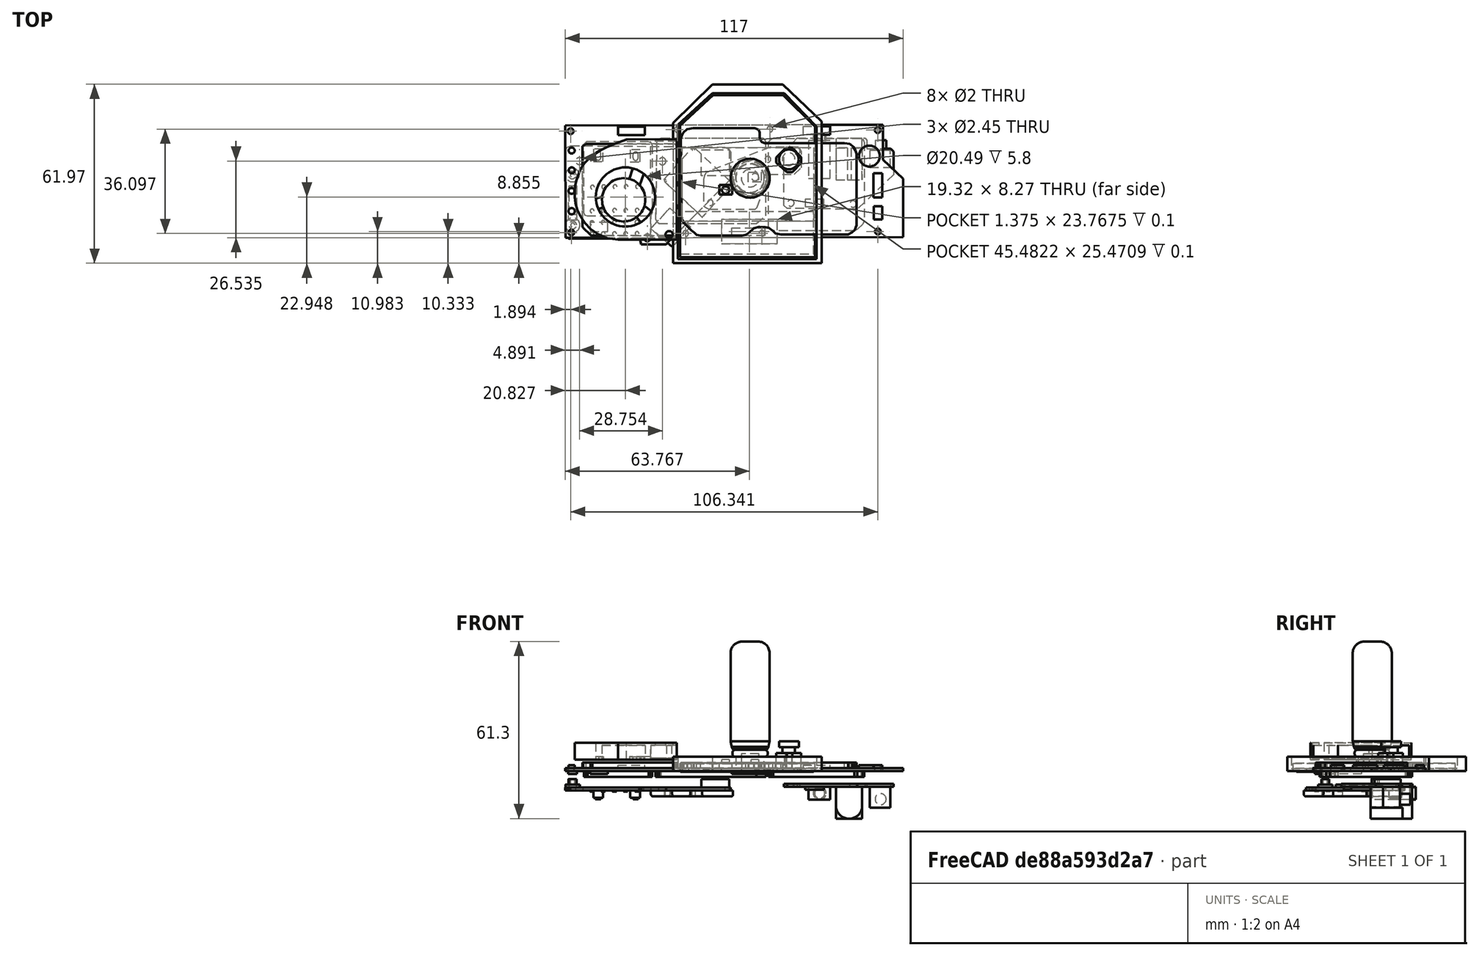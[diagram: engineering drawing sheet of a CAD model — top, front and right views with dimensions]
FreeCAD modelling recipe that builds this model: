
FCSTD DOCUMENT  (FreeCAD 0.19R24267 +99 (Git))
Label: v2PCB
License: All rights reserved
LicenseURL: http://en.wikipedia.org/wiki/All_rights_reserved
objects: Sketcher::SketchObject×41, PartDesign::Pad×35, Image::ImagePlane×9, PartDesign::Pocket×9, PartDesign::Body×8, PartDesign::Fillet×6, PartDesign::Chamfer×3, Mesh::Feature×1
note: 155 computed .brp shape members not serialized (recipe doc carries the construction recipe); baked Part::Feature solids carry a one-line shape summary decoded from their .brp

FEATURE [Image::ImagePlane] ImagePlane
  Placement = pos=(0,0,0) rot=(0,0,1;0.003491rad)
  XSize = 195.643
  YSize = 146.825
FEATURE [Sketcher::SketchObject] Sketch
  FullyConstrained = false
  MapMode = 5
  Support = -> [XY_Plane]
  sketch-geometry (14):
    g0: LineSegment StartX=-53.023 StartY=20.4074 StartZ=0 EndX=-52.9788 EndY=0.202758 EndZ=0
    g1: LineSegment StartX=-52.9788 StartY=0.202758 StartZ=0 EndX=-46.0602 EndY=-6.3752 EndZ=0
    g2: LineSegment StartX=-46.0602 StartY=-6.3752 StartZ=0 EndX=-46.0602 EndY=-18.4974 EndZ=0
    g3: LineSegment StartX=-46.0602 StartY=-18.4974 StartZ=0 EndX=63.9761 EndY=-18.2567 EndZ=0
    g4: LineSegment StartX=63.9761 StartY=-18.2567 StartZ=0 EndX=63.8909 EndY=20.6632 EndZ=0
    g5: LineSegment StartX=63.8909 StartY=20.6632 StartZ=0 EndX=-53.023 EndY=20.4074 EndZ=0
    g6: Circle CenterX=-44.2552 CenterY=18.4624 CenterZ=0 NormalX=0 NormalY=0 NormalZ=1 AngleXU=0 Radius=1
    g7: Circle CenterX=61.8709 CenterY=18.8233 CenterZ=0 NormalX=0 NormalY=0 NormalZ=1 AngleXU=0 Radius=1
    g8: Circle CenterX=62.0861 CenterY=-16.2831 CenterZ=0 NormalX=0 NormalY=0 NormalZ=1 AngleXU=0 Radius=1
    g9: Circle CenterX=25.1233 CenterY=-16.8581 CenterZ=0 NormalX=0 NormalY=0 NormalZ=1 AngleXU=0 Radius=1
    g10: Circle CenterX=-6.87654 CenterY=-16.9797 CenterZ=0 NormalX=0 NormalY=0 NormalZ=1 AngleXU=0 Radius=1
    g11: Circle CenterX=-44.1832 CenterY=-16.667 CenterZ=0 NormalX=0 NormalY=0 NormalZ=1 AngleXU=0 Radius=1
    g12: Circle CenterX=-4.12317 CenterY=19.0574 CenterZ=0 NormalX=0 NormalY=0 NormalZ=1 AngleXU=0 Radius=1
    g13: Circle CenterX=22.3007 CenterY=19.1172 CenterZ=0 NormalX=0 NormalY=0 NormalZ=1 AngleXU=0 Radius=1
  constraints (12):
    c: Coincident(g0,g1)
    c: Coincident(g1,g2)
    c: Vertical(g2)
    c: Coincident(g2,g3)
    c: Coincident(g3,g4)
    c: Coincident(g4,g5)
    c: Coincident(g5,g0)
    c: Parallel(g5,g3)
    c: DistanceX(g0) = -53.023
    c: DistanceY(g0) = 20.4074
    c: Perpendicular(g5,g0)
    c: Parallel(g4,g0)
FEATURE [PartDesign::Pad] Pad
  Direction = (1,1,1)
  Length = 1.1
  Length2 = 100
  Profile = -> Sketch
  Type = 0
FEATURE [Sketcher::SketchObject] Sketch001
  FullyConstrained = false
  MapMode = 5
  Support = -> [XY_Plane]
  sketch-geometry (61):
    g0: LineSegment StartX=-36.8446 StartY=16.2765 StartZ=0 EndX=-36.1772 EndY=17.9834 EndZ=0
    g1: LineSegment StartX=-36.1772 StartY=17.9834 StartZ=0 EndX=-35.306 EndY=18.7577 EndZ=0
    g2: LineSegment StartX=-35.306 StartY=18.7577 StartZ=0 EndX=-33.9509 EndY=19.5321 EndZ=0
    g3: LineSegment StartX=-33.9509 StartY=19.5321 StartZ=0 EndX=-10.7286 EndY=19.5321 EndZ=0
    g4: LineSegment StartX=-10.7286 StartY=19.5321 StartZ=0 EndX=-8.78697 EndY=19.1207 EndZ=0
    g5: LineSegment StartX=-8.78697 StartY=19.1207 StartZ=0 EndX=-7.91522 EndY=18.249 EndZ=0
    g6: LineSegment StartX=-7.91522 StartY=18.249 StartZ=0 EndX=-6.44909 EndY=17.1791 EndZ=0
    g7: LineSegment StartX=-6.44909 StartY=17.1791 StartZ=0 EndX=-5.18108 EndY=16.9413 EndZ=0
    g8: LineSegment StartX=-5.18108 StartY=16.9413 StartZ=0 EndX=-3.1602 EndY=16.8225 EndZ=0
    g9: LineSegment StartX=-3.1602 StartY=16.8225 StartZ=0 EndX=-1.29782 EndY=17.3772 EndZ=0
    g10: LineSegment StartX=-1.29782 StartY=17.3772 StartZ=0 EndX=0.401002 EndY=18.8142 EndZ=0
    g11: LineSegment StartX=0.401002 StartY=18.8142 StartZ=0 EndX=1.4716 EndY=19.5604 EndZ=0
    g12: LineSegment StartX=1.4716 StartY=19.5604 StartZ=0 EndX=2.70441 EndY=19.8848 EndZ=0
    g13: LineSegment StartX=2.70441 StartY=19.8848 StartZ=0 EndX=17.0749 EndY=19.8848 EndZ=0
    g14: LineSegment StartX=17.0749 StartY=19.8848 StartZ=0 EndX=18.5348 EndY=19.5644 EndZ=0
    g15: LineSegment StartX=18.5348 StartY=19.5644 StartZ=0 EndX=19.3134 EndY=18.9155 EndZ=0
    g16: LineSegment StartX=19.3134 StartY=18.9155 StartZ=0 EndX=20.3191 EndY=18.1044 EndZ=0
    g17: LineSegment StartX=20.3191 StartY=18.1044 StartZ=0 EndX=21.5195 EndY=16.8716 EndZ=0
    g18: LineSegment StartX=21.5195 StartY=16.8716 StartZ=0 EndX=22.8498 EndY=15.569 EndZ=0
    g19: LineSegment StartX=22.8498 StartY=15.569 StartZ=0 EndX=23.4607 EndY=14.5331 EndZ=0
    g20: LineSegment StartX=23.4607 StartY=14.5331 StartZ=0 EndX=23.7263 EndY=13.0722 EndZ=0
    g21: LineSegment StartX=23.7263 StartY=13.0722 StartZ=0 EndX=25.0278 EndY=13.0722 EndZ=0
    g22: LineSegment StartX=25.0278 StartY=13.0722 StartZ=0 EndX=25.0278 EndY=18.1699 EndZ=0
    g23: LineSegment StartX=25.0278 StartY=18.1699 StartZ=0 EndX=25.2082 EndY=19.0134 EndZ=0
    g24: LineSegment StartX=25.2082 StartY=19.0134 StartZ=0 EndX=25.6624 EndY=19.565 EndZ=0
    g25: LineSegment StartX=25.6624 StartY=19.565 StartZ=0 EndX=26.2464 EndY=19.8894 EndZ=0
    g26: LineSegment StartX=26.2464 StartY=19.8894 StartZ=0 EndX=54.5296 EndY=19.8894 EndZ=0
    g27: LineSegment StartX=54.5296 StartY=19.8894 StartZ=0 EndX=54.9473 EndY=19.84 EndZ=0
    g28: LineSegment StartX=54.9473 StartY=19.84 StartZ=0 EndX=55.2696 EndY=19.6371 EndZ=0
    g29: LineSegment StartX=55.2696 StartY=19.6371 StartZ=0 EndX=57.764 EndY=17.2382 EndZ=0
    g30: LineSegment StartX=57.764 StartY=17.2382 StartZ=0 EndX=58.0385 EndY=16.6415 EndZ=0
    g31: LineSegment StartX=58.0385 StartY=16.6415 StartZ=0 EndX=58.0623 EndY=16.2476 EndZ=0
    g32: LineSegment StartX=58.0623 StartY=16.2476 StartZ=0 EndX=58.0623 EndY=-10.4127 EndZ=0
    g33: LineSegment StartX=58.0623 StartY=-10.4127 StartZ=0 EndX=57.9614 EndY=-11.0869 EndZ=0
    g34: LineSegment StartX=57.9614 StartY=-11.0869 StartZ=0 EndX=57.5315 EndY=-11.4289 EndZ=0
    g35: LineSegment StartX=57.5315 StartY=-11.4289 StartZ=0 EndX=56.7107 EndY=-11.8882 EndZ=0
    g36: LineSegment StartX=56.7107 StartY=-11.8882 StartZ=0 EndX=26.8243 EndY=-11.8882 EndZ=0
    g37: LineSegment StartX=26.8243 StartY=-11.8882 StartZ=0 EndX=25.8681 EndY=-11.7722 EndZ=0
    g38: LineSegment StartX=25.8681 StartY=-11.7722 StartZ=0 EndX=25.3103 EndY=-11.0816 EndZ=0
    g39: LineSegment StartX=25.3103 StartY=-11.0816 StartZ=0 EndX=25.0978 EndY=-10.3645 EndZ=0
    g40: LineSegment StartX=25.0978 StartY=-10.3645 StartZ=0 EndX=23.9557 EndY=-10.4441 EndZ=0
    g41: LineSegment StartX=23.9557 StartY=-10.4441 StartZ=0 EndX=23.9557 EndY=-13.8325 EndZ=0
    g42: LineSegment StartX=23.9557 StartY=-13.8325 StartZ=0 EndX=23.6148 EndY=-14.7887 EndZ=0
    g43: LineSegment StartX=23.6148 StartY=-14.7887 StartZ=0 EndX=23.057 EndY=-15.8512 EndZ=0
    g44: LineSegment StartX=23.057 StartY=-15.8512 StartZ=0 EndX=21.8351 EndY=-16.9136 EndZ=0
    g45: LineSegment StartX=21.8351 StartY=-16.9136 StartZ=0 EndX=19.6168 EndY=-17.3676 EndZ=0
    g46: LineSegment StartX=19.6168 StartY=-17.3676 StartZ=0 EndX=16.8333 EndY=-17.3676 EndZ=0
    g47: LineSegment StartX=16.8333 StartY=-17.3676 StartZ=0 EndX=4.71408 EndY=-17.3676 EndZ=0
    g48: LineSegment StartX=4.71408 StartY=-17.3676 StartZ=0 EndX=-1.58584 EndY=-17.3676 EndZ=0
    g49: LineSegment StartX=-1.58584 StartY=-17.3676 StartZ=0 EndX=-2.89259 EndY=-16.8664 EndZ=0
    g50: LineSegment StartX=-2.89259 StartY=-16.8664 StartZ=0 EndX=-3.37658 EndY=-15.8501 EndZ=0
    g51: LineSegment StartX=-3.37658 StartY=-15.8501 StartZ=0 EndX=-3.37658 EndY=-14.1227 EndZ=0
    g52: LineSegment StartX=-3.37658 StartY=-14.1227 StartZ=0 EndX=-3.59208 EndY=-13.1169 EndZ=0
    g53: LineSegment StartX=-3.59208 StartY=-13.1169 StartZ=0 EndX=-4.1436 EndY=-12.533 EndZ=0
    g54: LineSegment StartX=-4.1436 StartY=-12.533 StartZ=0 EndX=-5.14931 EndY=-12.1437 EndZ=0
    g55: LineSegment StartX=-5.14931 StartY=-12.1437 StartZ=0 EndX=-32.6772 EndY=-12.1437 EndZ=0
    g56: LineSegment StartX=-32.6772 StartY=-12.1437 StartZ=0 EndX=-34.5589 EndY=-11.868 EndZ=0
    g57: LineSegment StartX=-34.5589 StartY=-11.868 StartZ=0 EndX=-35.6619 EndY=-10.8947 EndZ=0
    g58: LineSegment StartX=-35.6619 StartY=-10.8947 StartZ=0 EndX=-36.5054 EndY=-9.5646 EndZ=0
    g59: LineSegment StartX=-36.5054 StartY=-9.5646 StartZ=0 EndX=-36.8446 EndY=-8.44037 EndZ=0
    g60: LineSegment StartX=-36.8446 StartY=-8.44037 StartZ=0 EndX=-36.8446 EndY=16.2765 EndZ=0
  constraints (75):
    c: Coincident(g0,g1)
    c: Coincident(g1,g2)
    c: Coincident(g2,g3)
    c: Horizontal(g3)
    c: Coincident(g3,g4)
    c: Coincident(g4,g5)
    c: Coincident(g5,g6)
    c: Coincident(g6,g7)
    c: Coincident(g7,g8)
    c: Coincident(g8,g9)
    c: Coincident(g9,g10)
    c: Coincident(g10,g11)
    c: Coincident(g11,g12)
    c: Coincident(g12,g13)
    c: Horizontal(g13)
    c: Coincident(g13,g14)
    c: Coincident(g14,g15)
    c: Coincident(g15,g16)
    c: Coincident(g16,g17)
    c: Coincident(g17,g18)
    c: Coincident(g18,g19)
    c: Coincident(g19,g20)
    c: Coincident(g20,g21)
    c: Horizontal(g21)
    c: Coincident(g21,g22)
    c: Vertical(g22)
    c: Coincident(g22,g23)
    c: Coincident(g23,g24)
    c: Coincident(g24,g25)
    c: Coincident(g25,g26)
    c: Horizontal(g26)
    c: Coincident(g26,g27)
    c: Coincident(g27,g28)
    c: Coincident(g28,g29)
    c: Coincident(g29,g30)
    c: Coincident(g30,g31)
    c: Coincident(g31,g32)
    c: Vertical(g32)
    c: Coincident(g32,g33)
    c: Coincident(g33,g34)
    c: Coincident(g34,g35)
    c: Coincident(g35,g36)
    c: Horizontal(g36)
    c: Coincident(g36,g37)
    c: Coincident(g37,g38)
    c: Coincident(g38,g39)
    c: Coincident(g39,g40)
    c: Coincident(g40,g41)
    c: Vertical(g41)
    c: Coincident(g41,g42)
    c: Coincident(g42,g43)
    c: Coincident(g43,g44)
    c: Coincident(g44,g45)
    c: Coincident(g45,g46)
    c: Horizontal(g46)
    c: Coincident(g46,g47)
    c: Horizontal(g47)
    c: Coincident(g47,g48)
    c: Horizontal(g48)
    c: Coincident(g48,g49)
    c: Coincident(g49,g50)
    c: Coincident(g50,g51)
    c: Vertical(g51)
    c: Coincident(g51,g52)
    c: Coincident(g52,g53)
    c: Coincident(g53,g54)
    c: Coincident(g54,g55)
    c: Horizontal(g55)
    c: Coincident(g55,g56)
    c: Coincident(g56,g57)
    c: Coincident(g57,g58)
    c: Coincident(g58,g59)
    c: Coincident(g59,g60)
    c: Coincident(g60,g0)
    c: Vertical(g60)
FEATURE [PartDesign::Pad] Pad001
  BaseFeature = -> Pad
  Direction = (1,1,1)
  Length = 3
  Length2 = 100
  Profile = -> Sketch001
  Type = 0
FEATURE [Sketcher::SketchObject] Sketch002
  FullyConstrained = false
  MapMode = 5
  Placement = pos=(0,0,1.1) rot=(0,0,1;0rad)
  Support = -> [Pad001]
  sketch-geometry (21):
    g0: LineSegment StartX=-45.7157 StartY=14.2806 StartZ=0 EndX=-42.7834 EndY=14.2806 EndZ=0
    g1: LineSegment StartX=-42.7834 StartY=14.2806 StartZ=0 EndX=-42.7834 EndY=9.68408 EndZ=0
    g2: LineSegment StartX=-42.7834 StartY=9.68408 StartZ=0 EndX=-45.7157 EndY=9.68408 EndZ=0
    g3: LineSegment StartX=-45.7157 StartY=9.68408 StartZ=0 EndX=-45.7157 EndY=14.2806 EndZ=0
    g4: LineSegment StartX=-45.7553 StartY=6.63294 StartZ=0 EndX=-42.7042 EndY=6.63294 EndZ=0
    g5: LineSegment StartX=-42.7042 StartY=6.63294 StartZ=0 EndX=-42.7042 EndY=-1.68834 EndZ=0
    g6: LineSegment StartX=-42.7042 StartY=-1.68834 StartZ=0 EndX=-45.7553 EndY=-1.68834 EndZ=0
    g7: LineSegment StartX=-45.7553 StartY=-1.68834 StartZ=0 EndX=-45.7553 EndY=6.63294 EndZ=0
    g8: Circle CenterX=-41.3019 CenterY=-7.65171 CenterZ=0 NormalX=0 NormalY=0 NormalZ=1 AngleXU=0 Radius=3.62162
    g9: Circle CenterX=61.7609 CenterY=11.4352 CenterZ=0 NormalX=0 NormalY=0 NormalZ=1 AngleXU=0 Radius=1.0872
    g10: Circle CenterX=61.7934 CenterY=4.39516 CenterZ=0 NormalX=0 NormalY=0 NormalZ=1 AngleXU=0 Radius=1.03866
    g11: Circle CenterX=61.7273 CenterY=-2.72566 CenterZ=0 NormalX=0 NormalY=0 NormalZ=1 AngleXU=0 Radius=1.03866
    g12: Circle CenterX=61.7408 CenterY=-9.57455 CenterZ=0 NormalX=0 NormalY=0 NormalZ=1 AngleXU=0 Radius=1.03866
    g13: LineSegment StartX=-27.7059 StartY=-15.0443 StartZ=0 EndX=-18.4201 EndY=-15.0443 EndZ=0
    g14: LineSegment StartX=-18.4201 StartY=-15.0443 StartZ=0 EndX=-18.4201 EndY=-17.9821 EndZ=0
    g15: LineSegment StartX=-18.4201 StartY=-17.9821 StartZ=0 EndX=-27.7059 EndY=-17.9821 EndZ=0
    g16: LineSegment StartX=-27.7059 StartY=-17.9821 StartZ=0 EndX=-27.7059 EndY=-15.0443 EndZ=0
    g17: LineSegment StartX=36.3929 StartY=-14.8666 StartZ=0 EndX=45.7202 EndY=-14.8666 EndZ=0
    g18: LineSegment StartX=45.7202 StartY=-14.8666 StartZ=0 EndX=45.7202 EndY=-17.8222 EndZ=0
    g19: LineSegment StartX=45.7202 StartY=-17.8222 StartZ=0 EndX=36.3929 EndY=-17.8222 EndZ=0
    g20: LineSegment StartX=36.3929 StartY=-17.8222 StartZ=0 EndX=36.3929 EndY=-14.8666 EndZ=0
  constraints (32):
    c: Coincident(g0,g1)
    c: Coincident(g1,g2)
    c: Coincident(g2,g3)
    c: Coincident(g3,g0)
    c: Horizontal(g0)
    c: Horizontal(g2)
    c: Vertical(g1)
    c: Vertical(g3)
    c: Coincident(g4,g5)
    c: Coincident(g5,g6)
    c: Coincident(g6,g7)
    c: Coincident(g7,g4)
    c: Horizontal(g4)
    c: Horizontal(g6)
    c: Vertical(g5)
    c: Vertical(g7)
    c: Coincident(g13,g14)
    c: Coincident(g14,g15)
    c: Coincident(g15,g16)
    c: Coincident(g16,g13)
    c: Horizontal(g13)
    c: Horizontal(g15)
    c: Vertical(g14)
    c: Vertical(g16)
    c: Coincident(g17,g18)
    c: Coincident(g18,g19)
    c: Coincident(g19,g20)
    c: Coincident(g20,g17)
    c: Horizontal(g17)
    c: Horizontal(g19)
    c: Vertical(g18)
    c: Vertical(g20)
FEATURE [PartDesign::Pad] Pad002
  BaseFeature = -> Pad001
  Direction = (1,1,1)
  Length = 1
  Length2 = 100
  Profile = -> Sketch002
  Type = 0
FEATURE [Sketcher::SketchObject] Sketch003
  FullyConstrained = false
  MapMode = 5
  Placement = pos=(0,0,3) rot=(0,0,1;0rad)
  Support = -> [Pad002]
  sketch-geometry (4):
    g0: LineSegment StartX=23.7352 StartY=13.1919 StartZ=0 EndX=23.9822 EndY=-10.5289 EndZ=0
    g1: LineSegment StartX=23.9822 StartY=-10.5289 StartZ=0 EndX=25.1102 EndY=-10.5289 EndZ=0
    g2: LineSegment StartX=25.1102 StartY=-10.5289 StartZ=0 EndX=25.0187 EndY=13.2386 EndZ=0
    g3: LineSegment StartX=25.0187 StartY=13.2386 StartZ=0 EndX=23.7352 EndY=13.1919 EndZ=0
  constraints (5):
    c: Coincident(g0,g1)
    c: Horizontal(g1)
    c: Coincident(g1,g2)
    c: Coincident(g2,g3)
    c: Coincident(g3,g0)
FEATURE [PartDesign::Pocket] Pocket
  BaseFeature = -> Pad002
  Length = 2
  Length2 = 100
  Profile = -> Sketch003
  Type = 0
FEATURE [Image::ImagePlane] ImagePlane001
  Placement = pos=(6.7,2,0) rot=(-1,0,0;3.14159rad)
  XSize = 196.671
  YSize = 147.597
FEATURE [Sketcher::SketchObject] Sketch004
  FullyConstrained = false
  MapMode = 5
  Placement = pos=(0,0,0) rot=(1,0,0;3.14159rad)
  Support = -> [Pocket]
  sketch-geometry (37):
    g0: LineSegment StartX=-38.3718 StartY=13.8148 StartZ=0 EndX=-39.0172 EndY=13.3602 EndZ=0
    g1: LineSegment StartX=-39.0172 StartY=13.3602 StartZ=0 EndX=-39.4107 EndY=12.8136 EndZ=0
    g2: LineSegment StartX=-39.4107 StartY=12.8136 StartZ=0 EndX=-39.52 EndY=12.4201 EndZ=0
    g3: LineSegment StartX=-39.52 StartY=12.4201 StartZ=0 EndX=-39.52 EndY=-14.6845 EndZ=0
    g4: LineSegment StartX=-39.52 StartY=-14.6845 StartZ=0 EndX=-38.9803 EndY=-15.9239 EndZ=0
    g5: LineSegment StartX=-38.9803 StartY=-15.9239 StartZ=0 EndX=-37.056 EndY=-17.6525 EndZ=0
    g6: LineSegment StartX=-37.056 StartY=-17.6525 StartZ=0 EndX=-36.1428 EndY=-18.1744 EndZ=0
    g7: LineSegment StartX=-36.1428 StartY=-18.1744 StartZ=0 EndX=-8.00073 EndY=-18.1744 EndZ=0
    g8: LineSegment StartX=-8.00073 StartY=-18.1744 StartZ=0 EndX=-7.08768 EndY=-17.713 EndZ=0
    g9: LineSegment StartX=-7.08768 StartY=-17.713 StartZ=0 EndX=-6.31843 EndY=-17.0145 EndZ=0
    g10: LineSegment StartX=-6.31843 StartY=-17.0145 StartZ=0 EndX=-6.31843 EndY=12.3493 EndZ=0
    g11: LineSegment StartX=-6.31843 StartY=12.3493 StartZ=0 EndX=-6.70782 EndY=12.9208 EndZ=0
    g12: LineSegment StartX=-6.70782 StartY=12.9208 StartZ=0 EndX=-7.17678 EndY=13.4337 EndZ=0
    g13: LineSegment StartX=-7.17678 StartY=13.4337 StartZ=0 EndX=-7.73367 EndY=13.8148 EndZ=0
    g14: LineSegment StartX=-7.73367 StartY=13.8148 StartZ=0 EndX=-38.3718 EndY=13.8148 EndZ=0
    g15: LineSegment StartX=-5.50407 StartY=12.5862 StartZ=0 EndX=-5.05245 EndY=13.2897 EndZ=0
    g16: LineSegment StartX=-5.05245 StartY=13.2897 StartZ=0 EndX=-4.55126 EndY=13.7372 EndZ=0
    g17: LineSegment StartX=-4.55126 StartY=13.7372 StartZ=0 EndX=30.8305 EndY=13.7372 EndZ=0
    g18: LineSegment StartX=30.8305 StartY=13.7372 StartZ=0 EndX=31.5738 EndY=13.5845 EndZ=0
    g19: LineSegment StartX=31.5738 StartY=13.5845 StartZ=0 EndX=32.339 EndY=12.6663 EndZ=0
    g20: LineSegment StartX=32.339 StartY=12.6663 StartZ=0 EndX=32.7019 EndY=-14.1785 EndZ=0
    g21: LineSegment StartX=32.7019 StartY=-14.1785 StartZ=0 EndX=32.2884 EndY=-15.0677 EndZ=0
    g22: LineSegment StartX=32.2884 StartY=-15.0677 StartZ=0 EndX=31.5123 EndY=-15.6473 EndZ=0
    g23: LineSegment StartX=31.5123 StartY=-15.6473 StartZ=0 EndX=-2.13722 EndY=-15.6473 EndZ=0
    g24: LineSegment StartX=-2.13722 StartY=-15.6473 StartZ=0 EndX=-5.50407 EndY=-13.009 EndZ=0
    g25: LineSegment StartX=-5.50407 StartY=-13.009 StartZ=0 EndX=-5.50407 EndY=12.5862 EndZ=0
    g26: LineSegment StartX=33.8245 StartY=-11.8303 StartZ=0 EndX=34.2779 EndY=-12.7966 EndZ=0
    g27: LineSegment StartX=34.2779 StartY=-12.7966 StartZ=0 EndX=35.0834 EndY=-13.1367 EndZ=0
    g28: LineSegment StartX=35.0834 StartY=-13.1367 StartZ=0 EndX=56.2902 EndY=-13.1367 EndZ=0
    g29: LineSegment StartX=56.2902 StartY=-13.1367 StartZ=0 EndX=57.1647 EndY=-12.835 EndZ=0
    g30: LineSegment StartX=57.1647 StartY=-12.835 StartZ=0 EndX=57.4926 EndY=-12.0261 EndZ=0
    g31: LineSegment StartX=57.4926 StartY=-12.0261 StartZ=0 EndX=57.4926 EndY=11.7012 EndZ=0
    g32: LineSegment StartX=57.4926 StartY=11.7012 StartZ=0 EndX=56.4474 EndY=12.796 EndZ=0
    g33: LineSegment StartX=56.4474 StartY=12.796 StartZ=0 EndX=35.3435 EndY=12.796 EndZ=0
    g34: LineSegment StartX=35.3435 StartY=12.796 StartZ=0 EndX=34.3766 EndY=12.3259 EndZ=0
    g35: LineSegment StartX=34.3766 StartY=12.3259 StartZ=0 EndX=33.8245 EndY=11.4115 EndZ=0
    g36: LineSegment StartX=33.8245 StartY=11.4115 StartZ=0 EndX=33.8245 EndY=-11.8303 EndZ=0
  constraints (48):
    c: Coincident(g0,g1)
    c: Coincident(g1,g2)
    c: Coincident(g2,g3)
    c: Vertical(g3)
    c: Coincident(g3,g4)
    c: Coincident(g4,g5)
    c: Coincident(g5,g6)
    c: Coincident(g6,g7)
    c: Horizontal(g7)
    c: Coincident(g7,g8)
    c: Coincident(g8,g9)
    c: Coincident(g9,g10)
    c: Vertical(g10)
    c: Coincident(g10,g11)
    c: Coincident(g11,g12)
    c: Coincident(g12,g13)
    c: Coincident(g13,g14)
    c: Coincident(g14,g0)
    c: Horizontal(g14)
    c: Coincident(g15,g16)
    c: Coincident(g16,g17)
    c: Horizontal(g17)
    c: Coincident(g17,g18)
    c: Coincident(g18,g19)
    c: Coincident(g19,g20)
    c: Coincident(g20,g21)
    c: Coincident(g21,g22)
    c: Coincident(g22,g23)
    c: Horizontal(g23)
    c: Coincident(g23,g24)
    c: Coincident(g24,g25)
    c: Coincident(g25,g15)
    c: Vertical(g25)
    c: Coincident(g26,g27)
    c: Coincident(g27,g28)
    c: Horizontal(g28)
    c: Coincident(g28,g29)
    c: Coincident(g29,g30)
    c: Coincident(g30,g31)
    c: Vertical(g31)
    c: Coincident(g31,g32)
    c: Coincident(g32,g33)
    c: Horizontal(g33)
    c: Coincident(g33,g34)
    c: Coincident(g34,g35)
    c: Coincident(g35,g36)
    c: Coincident(g36,g26)
    c: Vertical(g36)
FEATURE [PartDesign::Pad] Pad003
  BaseFeature = -> Pocket
  Direction = (1,1,1)
  Length = 2
  Length2 = 100
  Profile = -> Sketch004
  Type = 0
FEATURE [Sketcher::SketchObject] Sketch005
  FullyConstrained = false
  MapMode = 5
  Placement = pos=(0,0,0) rot=(1,0,0;3.14159rad)
  Support = -> [Pad003]
  sketch-geometry (8):
    g0: LineSegment StartX=59.9182 StartY=-3.71203 StartZ=0 EndX=62.984 EndY=-3.71203 EndZ=0
    g1: LineSegment StartX=62.984 StartY=-3.71203 StartZ=0 EndX=62.984 EndY=-14.3772 EndZ=0
    g2: LineSegment StartX=62.984 StartY=-14.3772 StartZ=0 EndX=59.9182 EndY=-14.3772 EndZ=0
    g3: LineSegment StartX=59.9182 StartY=-14.3772 StartZ=0 EndX=59.9182 EndY=-3.71203 EndZ=0
    g4: LineSegment StartX=49.2016 StartY=-15.2468 StartZ=0 EndX=55.3231 EndY=-15.2468 EndZ=0
    g5: LineSegment StartX=55.3231 StartY=-15.2468 StartZ=0 EndX=55.3231 EndY=-18.4388 EndZ=0
    g6: LineSegment StartX=55.3231 StartY=-18.4388 StartZ=0 EndX=49.2016 EndY=-18.4388 EndZ=0
    g7: LineSegment StartX=49.2016 StartY=-18.4388 StartZ=0 EndX=49.2016 EndY=-15.2468 EndZ=0
  constraints (16):
    c: Coincident(g0,g1)
    c: Coincident(g1,g2)
    c: Coincident(g2,g3)
    c: Coincident(g3,g0)
    c: Horizontal(g0)
    c: Horizontal(g2)
    c: Vertical(g1)
    c: Vertical(g3)
    c: Coincident(g4,g5)
    c: Coincident(g5,g6)
    c: Coincident(g6,g7)
    c: Coincident(g7,g4)
    c: Horizontal(g4)
    c: Horizontal(g6)
    c: Vertical(g5)
    c: Vertical(g7)
FEATURE [PartDesign::Pad] Pad004
  BaseFeature = -> Pad003
  Direction = (1,1,1)
  Length = 1
  Length2 = 100
  Profile = -> Sketch005
  Type = 0
FEATURE [PartDesign::Body] Body  label="主板"
  Group = -> [Sketch,Pad,Sketch001,Pad001,Sketch002,Pad002,Sketch003,Pocket,Sketch004,Pad003,Sketch005,Pad004]
  Origin = -> Origin
  Placement = pos=(0,0,0) rot=(0,0,1;3.14159rad)
  Tip = -> Pad004
FEATURE [Image::ImagePlane] ImagePlane002
  Placement = pos=(-0.07487,-3.89928,0) rot=(0,0,1;6.26399rad)
  XSize = 121.534
  YSize = 162.205
FEATURE [Sketcher::SketchObject] Sketch006
  FullyConstrained = false
  MapMode = 5
  Support = -> [XY_Plane001]
  sketch-geometry (18):
    g0: LineSegment StartX=-18.4256 StartY=-1.34093 StartZ=0 EndX=-18.4099 EndY=-21.5909 EndZ=0
    g1: LineSegment StartX=-18.4099 StartY=-21.5909 StartZ=0 EndX=16.4943 EndY=-21.5976 EndZ=0
    g2: LineSegment StartX=16.4943 StartY=-21.5976 StartZ=0 EndX=16.2785 EndY=-4.27596 EndZ=0
    g3-g9: Circle x7 (B-spline internal-alignment scaffolding for g10; pole/knot coordinates omitted)
    g10: BSplineCurve PolesCount=7 KnotsCount=5 Degree=3 IsPeriodic=0
    g11-g15: GeomPoint x5 (B-spline internal-alignment scaffolding for g10; pole/knot coordinates omitted)
    g16: Circle CenterX=-3.60227 CenterY=-3.84748 CenterZ=0 NormalX=0 NormalY=0 NormalZ=1 AngleXU=0 Radius=10.2437
    g17: Circle CenterX=-16.6253 CenterY=-18.983 CenterZ=0 NormalX=0 NormalY=0 NormalZ=1 AngleXU=0 Radius=1.2374
  constraints (8):
    c: Coincident(g0,g1)
    c: Coincident(g1,g2)
    c: Coincident(g10,g0)
    c: Weight(g3) = 1
    c: Equal(g3, g4-g9) x6
    c: Coincident(g10,g2)
    c: InternalAlignment(g3-g9 -> g10) x7
    c: InternalAlignment(g11-g15 -> g10) x5
FEATURE [PartDesign::Pad] Pad005
  Direction = (1,1,1)
  Length = 5.8
  Length2 = 100
  Profile = -> Sketch006
  Type = 0
FEATURE [Sketcher::SketchObject] Sketch007
  FullyConstrained = false
  MapMode = 5
  Support = -> [XY_Plane001]
  sketch-geometry (12):
    g0: LineSegment StartX=-8.07719 StartY=5.93515 StartZ=0 EndX=-7.1147 EndY=3.78717 EndZ=0
    g1: LineSegment StartX=-7.1147 StartY=3.78717 StartZ=0 EndX=-10.6829 EndY=-7.78344 EndZ=0
    g2: LineSegment StartX=-10.6829 StartY=-7.78344 StartZ=0 EndX=-12.9278 EndY=-9.78625 EndZ=0
    g3: LineSegment StartX=-12.9278 StartY=-9.78625 StartZ=0 EndX=-8.90015 EndY=-13.4177 EndZ=0
    g4: LineSegment StartX=-8.90015 StartY=-13.4177 StartZ=0 EndX=-6.14903 EndY=-9.72022 EndZ=0
    g5: LineSegment StartX=-6.14903 StartY=-9.72022 StartZ=0 EndX=0.343604 EndY=-8.79585 EndZ=0
    g6: LineSegment StartX=0.343604 StartY=-8.79585 StartZ=0 EndX=5.14155 EndY=-10.4685 EndZ=0
    g7: LineSegment StartX=5.14155 StartY=-10.4685 StartZ=0 EndX=6.92427 EndY=-6.55094 EndZ=0
    g8: LineSegment StartX=6.92427 StartY=-6.55094 StartZ=0 EndX=2.5445 EndY=-5.20839 EndZ=0
    g9: LineSegment StartX=2.5445 StartY=-5.20839 StartZ=0 EndX=-3.52084 EndY=4.17824 EndZ=0
    g10: LineSegment StartX=-3.52084 StartY=4.17824 StartZ=0 EndX=-4.27353 EndY=7.00082 EndZ=0
    g11: LineSegment StartX=-4.27353 StartY=7.00082 StartZ=0 EndX=-8.07719 EndY=5.93515 EndZ=0
  constraints (12):
    c: Coincident(g0,g1)
    c: Coincident(g1,g2)
    c: Coincident(g2,g3)
    c: Coincident(g3,g4)
    c: Coincident(g4,g5)
    c: Coincident(g5,g6)
    c: Coincident(g6,g7)
    c: Coincident(g7,g8)
    c: Coincident(g8,g9)
    c: Coincident(g9,g10)
    c: Coincident(g10,g11)
    c: Coincident(g11,g0)
FEATURE [PartDesign::Pad] Pad006
  BaseFeature = -> Pad005
  Direction = (1,1,1)
  Length = 1
  Length2 = 100
  Profile = -> Sketch007
  Type = 0
FEATURE [Sketcher::SketchObject] Sketch008
  FullyConstrained = false
  MapMode = 5
  Support = -> [XY_Plane001]
  sketch-geometry (1):
    g0: Circle CenterX=-4.58223 CenterY=-3.25776 CenterZ=0 NormalX=0 NormalY=0 NormalZ=1 AngleXU=0 Radius=7.50767
FEATURE [PartDesign::Pad] Pad007
  BaseFeature = -> Pad006
  Direction = (1,1,1)
  Length = 5
  Length2 = 100
  Profile = -> Sketch008
  Type = 0
FEATURE [Sketcher::SketchObject] Sketch009
  FullyConstrained = false
  MapMode = 5
  Placement = pos=(-0.00414761,-21.5944,0) rot=(1,-9.6e-05,-9.6e-05;1.5708rad)
  Support = -> [Pad007]
  sketch-geometry (4):
    g0: LineSegment StartX=-17.4999 StartY=4.98477 StartZ=0 EndX=15.6121 EndY=4.98477 EndZ=0
    g1: LineSegment StartX=15.6121 StartY=4.98477 StartZ=0 EndX=15.6121 EndY=0.522236 EndZ=0
    g2: LineSegment StartX=15.6121 StartY=0.522236 StartZ=0 EndX=-17.4999 EndY=0.522236 EndZ=0
    g3: LineSegment StartX=-17.4999 StartY=0.522236 StartZ=0 EndX=-17.4999 EndY=4.98477 EndZ=0
  constraints (8):
    c: Coincident(g0,g1)
    c: Coincident(g1,g2)
    c: Coincident(g2,g3)
    c: Coincident(g3,g0)
    c: Horizontal(g0)
    c: Horizontal(g2)
    c: Vertical(g1)
    c: Vertical(g3)
FEATURE [PartDesign::Pocket] Pocket001
  BaseFeature = -> Pad007
  Length = 9
  Length2 = 100
  Profile = -> Sketch009
  Type = 0
FEATURE [Image::ImagePlane] ImagePlane003
  Placement = pos=(-38.586,-1.05963,0) rot=(0,0,1;5.68105rad)
  XSize = 86.3057
  YSize = 115.188
FEATURE [Sketcher::SketchObject] Sketch010
  FullyConstrained = false
  MapMode = 5
  Support = -> [XY_Plane001]
  sketch-geometry (19):
    g0: LineSegment StartX=-12.5785 StartY=17.8069 StartZ=0 EndX=-13.4988 EndY=17.6922 EndZ=0
    g1: LineSegment StartX=-13.4988 StartY=17.6922 StartZ=0 EndX=-13.997 EndY=17.2533 EndZ=0
    g2: LineSegment StartX=-13.997 StartY=17.2533 StartZ=0 EndX=-14.302 EndY=16.3635 EndZ=0
    g3: LineSegment StartX=-14.302 StartY=16.3635 StartZ=0 EndX=-14.302 EndY=-37.2801 EndZ=0
    g4: LineSegment StartX=-14.302 StartY=-37.2801 StartZ=0 EndX=-13.2209 EndY=-38.705 EndZ=0
    g5: LineSegment StartX=-13.2209 StartY=-38.705 StartZ=0 EndX=-12.2719 EndY=-39.3456 EndZ=0
    g6: LineSegment StartX=-12.2719 StartY=-39.3456 StartZ=0 EndX=-3.15959 EndY=-39.3456 EndZ=0
    g7: LineSegment StartX=-3.15959 StartY=-39.3456 StartZ=0 EndX=19.7094 EndY=-16.8206 EndZ=0
    g8: LineSegment StartX=19.7094 StartY=-16.8206 StartZ=0 EndX=19.7094 EndY=-8.01852 EndZ=0
    g9: LineSegment StartX=19.7094 StartY=-8.01852 StartZ=0 EndX=17.9805 EndY=-8.01852 EndZ=0
    g10: LineSegment StartX=17.9805 StartY=-8.01852 StartZ=0 EndX=17.542 EndY=-7.66743 EndZ=0
    g11: LineSegment StartX=17.542 StartY=-7.66743 StartZ=0 EndX=17.7247 EndY=15.7466 EndZ=0
    g12: LineSegment StartX=17.7247 StartY=15.7466 StartZ=0 EndX=17.4327 EndY=16.8139 EndZ=0
    g13: LineSegment StartX=17.4327 StartY=16.8139 StartZ=0 EndX=16.9813 EndY=17.3298 EndZ=0
    g14: LineSegment StartX=16.9813 StartY=17.3298 StartZ=0 EndX=16.2344 EndY=17.8069 EndZ=0
    g15: LineSegment StartX=16.2344 StartY=17.8069 StartZ=0 EndX=-12.5785 EndY=17.8069 EndZ=0
    g16: Circle CenterX=-9.26571 CenterY=13.1333 CenterZ=0 NormalX=0 NormalY=0 NormalZ=1 AngleXU=0 Radius=1.17702
    g17: Circle CenterX=-9.15935 CenterY=-15.6504 CenterZ=0 NormalX=0 NormalY=0 NormalZ=1 AngleXU=0 Radius=1.16269
    g18: Circle CenterX=17.2835 CenterY=-10.4631 CenterZ=0 NormalX=0 NormalY=0 NormalZ=1 AngleXU=0 Radius=1.17702
  constraints (19):
    c: Coincident(g0,g1)
    c: Coincident(g1,g2)
    c: Coincident(g2,g3)
    c: Vertical(g3)
    c: Coincident(g4,g5)
    c: Coincident(g5,g6)
    c: Horizontal(g6)
    c: Coincident(g6,g7)
    c: Coincident(g7,g8)
    c: Vertical(g8)
    c: Coincident(g8,g9)
    c: Coincident(g9,g10)
    c: Coincident(g10,g11)
    c: Coincident(g11,g12)
    c: Coincident(g12,g13)
    c: Coincident(g13,g14)
    c: Coincident(g14,g15)
    c: Coincident(g15,g0)
    c: Horizontal(g15)
FEATURE [PartDesign::Body] Body001  label="风扇"
  Group = -> [Sketch006,Pad005,Sketch007,Pad006,Sketch008,Pad007,Sketch009,Pocket001,Sketch010]
  Origin = -> Origin001
  Placement = pos=(-47,-2.9,4) rot=(0,0,1;1.5708rad)
  Tip = -> Pocket001
FEATURE [Sketcher::SketchObject] Sketch011
  FullyConstrained = false
  MapMode = 5
  Support = -> [XY_Plane002]
  sketch-geometry (19):
    g0: LineSegment StartX=-64.8714 StartY=16.5247 StartZ=0 EndX=-64.9533 EndY=-12.7822 EndZ=0
    g1: LineSegment StartX=-64.9533 StartY=-12.7822 StartZ=0 EndX=-64.4659 EndY=-13.9509 EndZ=0
    g2: LineSegment StartX=-64.4659 StartY=-13.9509 StartZ=0 EndX=-63.0503 EndY=-14.5567 EndZ=0
    g3: LineSegment StartX=-63.0503 StartY=-14.5567 StartZ=0 EndX=-9.76927 EndY=-14.0982 EndZ=0
    g4: LineSegment StartX=-9.76927 StartY=-14.0982 StartZ=0 EndX=-8.39049 EndY=-13.46 EndZ=0
    g5: LineSegment StartX=-8.39049 StartY=-13.46 StartZ=0 EndX=-7.6536 EndY=-12.1974 EndZ=0
    g6: LineSegment StartX=-7.6536 StartY=-12.1974 StartZ=0 EndX=-7.8022 EndY=-2.91762 EndZ=0
    g7: LineSegment StartX=-7.8022 StartY=-2.91762 StartZ=0 EndX=-30.062 EndY=19.6175 EndZ=0
    g8: LineSegment StartX=-30.062 StartY=19.6175 StartZ=0 EndX=-38.7537 EndY=19.6175 EndZ=0
    g9: LineSegment StartX=-38.7537 StartY=19.6175 StartZ=0 EndX=-38.9127 EndY=18.4637 EndZ=0
    g10: LineSegment StartX=-38.9127 StartY=18.4637 StartZ=0 EndX=-39.3672 EndY=17.5692 EndZ=0
    g11: LineSegment StartX=-39.3672 StartY=17.5692 StartZ=0 EndX=-63.3589 EndY=17.6901 EndZ=0
    g12: LineSegment StartX=-63.3589 StartY=17.6901 StartZ=0 EndX=-64.1992 EndY=17.1789 EndZ=0
    g13: LineSegment StartX=-64.1992 StartY=17.1789 StartZ=0 EndX=-64.8714 EndY=16.5247 EndZ=0
    g14: Circle CenterX=-60.0894 CenterY=-9.23985 CenterZ=0 NormalX=0 NormalY=0 NormalZ=1 AngleXU=0 Radius=1.22431
    g15: Circle CenterX=-31.3356 CenterY=-9.16643 CenterZ=0 NormalX=0 NormalY=0 NormalZ=1 AngleXU=0 Radius=1.22431
    g16: Circle CenterX=-36.5524 CenterY=17.2953 CenterZ=0 NormalX=0 NormalY=0 NormalZ=1 AngleXU=0 Radius=1.22431
    g17: GeomPoint X=-20.6075 Y=10.0461 Z=0
    g18: GeomPoint X=-19.4339 Y=8.85794 Z=0
  constraints (17):
    c: Coincident(g0,g1)
    c: Coincident(g1,g2)
    c: Coincident(g2,g3)
    c: Coincident(g3,g4)
    c: Coincident(g4,g5)
    c: Coincident(g5,g6)
    c: Coincident(g6,g7)
    c: Coincident(g7,g8)
    c: Horizontal(g8)
    c: Coincident(g8,g9)
    c: Coincident(g9,g10)
    c: Coincident(g10,g11)
    c: Coincident(g11,g12)
    c: Coincident(g12,g13)
    c: Coincident(g13,g0)
    c: PointOnObject(g17,g7)
    c: PointOnObject(g18,g7)
FEATURE [PartDesign::Pad] Pad008
  Direction = (1,1,1)
  Length = 1
  Length2 = 100
  Profile = -> Sketch011
  Type = 0
FEATURE [Sketcher::SketchObject] Sketch012
  FullyConstrained = false
  MapMode = 5
  Placement = pos=(0,0,1) rot=(0,0,1;0rad)
  Support = -> [Pad008]
  sketch-geometry (10):
    g0: LineSegment StartX=-27.9862 StartY=20.438 StartZ=0 EndX=-35.3788 EndY=14.1911 EndZ=0
    g1: LineSegment StartX=-35.3788 StartY=14.1911 StartZ=0 EndX=-28.757 EndY=7.00259 EndZ=0
    g2: LineSegment StartX=-28.757 StartY=7.00259 StartZ=0 EndX=-21.6454 EndY=13.5738 EndZ=0
    g3: LineSegment StartX=-21.6454 StartY=13.5738 StartZ=0 EndX=-27.9862 EndY=20.438 EndZ=0
    g4: LineSegment StartX=-17.547 StartY=10.17 StartZ=0 EndX=-30.4221 EndY=-1.99924 EndZ=0
    g5: LineSegment StartX=-30.4221 StartY=-1.99924 StartZ=0 EndX=-30.7123 EndY=-2.99889 EndZ=0
    g6: LineSegment StartX=-30.7123 StartY=-2.99889 StartZ=0 EndX=-21.2284 EndY=-13.6039 EndZ=0
    g7: LineSegment StartX=-21.2284 StartY=-13.6039 StartZ=0 EndX=-20.0667 EndY=-13.6039 EndZ=0
    g8: LineSegment StartX=-20.0667 StartY=-13.6039 StartZ=0 EndX=-6.91266 EndY=-1.37025 EndZ=0
    g9: LineSegment StartX=-6.91266 StartY=-1.37025 StartZ=0 EndX=-17.547 EndY=10.17 EndZ=0
  constraints (11):
    c: Coincident(g0,g1)
    c: Coincident(g1,g2)
    c: Coincident(g2,g3)
    c: Coincident(g0,g3)
    c: Coincident(g4,g5)
    c: Coincident(g5,g6)
    c: Coincident(g6,g7)
    c: Horizontal(g7)
    c: Coincident(g7,g8)
    c: Coincident(g8,g9)
    c: Coincident(g9,g4)
FEATURE [PartDesign::Pad] Pad009
  BaseFeature = -> Pad008
  Direction = (1,1,1)
  Length = 2
  Length2 = 100
  Profile = -> Sketch012
  Type = 0
FEATURE [Sketcher::SketchObject] Sketch013
  FullyConstrained = false
  MapMode = 5
  Placement = pos=(0,0,1) rot=(0,0,1;0rad)
  Support = -> [Pad009]
  sketch-geometry (20):
    g0: Circle CenterX=-55.7125 CenterY=16.0865 CenterZ=0 NormalX=0 NormalY=0 NormalZ=1 AngleXU=0 Radius=0.669574
    g1: Circle CenterX=-51.8132 CenterY=15.9683 CenterZ=0 NormalX=0 NormalY=0 NormalZ=1 AngleXU=0 Radius=0.669574
    g2: Circle CenterX=-47.9139 CenterY=15.9289 CenterZ=0 NormalX=0 NormalY=0 NormalZ=1 AngleXU=0 Radius=0.669574
    g3: Circle CenterX=-44.0541 CenterY=15.9289 CenterZ=0 NormalX=0 NormalY=0 NormalZ=1 AngleXU=0 Radius=0.669574
    g4: Circle CenterX=-40.1154 CenterY=15.8896 CenterZ=0 NormalX=0 NormalY=0 NormalZ=1 AngleXU=0 Radius=0.669574
    g5: Circle CenterX=-55.7315 CenterY=12.1033 CenterZ=0 NormalX=0 NormalY=0 NormalZ=1 AngleXU=0 Radius=0.669574
    g6: Circle CenterX=-51.8322 CenterY=11.9851 CenterZ=0 NormalX=0 NormalY=0 NormalZ=1 AngleXU=0 Radius=0.669574
    g7: Circle CenterX=-47.933 CenterY=11.9457 CenterZ=0 NormalX=0 NormalY=0 NormalZ=1 AngleXU=0 Radius=0.669574
    g8: Circle CenterX=-44.0731 CenterY=11.9457 CenterZ=0 NormalX=0 NormalY=0 NormalZ=1 AngleXU=0 Radius=0.669574
    g9: Circle CenterX=-40.1344 CenterY=11.9063 CenterZ=0 NormalX=0 NormalY=0 NormalZ=1 AngleXU=0 Radius=0.669574
    g10: Circle CenterX=-55.6688 CenterY=8.02524 CenterZ=0 NormalX=0 NormalY=0 NormalZ=1 AngleXU=0 Radius=0.669574
    g11: Circle CenterX=-51.7695 CenterY=7.90708 CenterZ=0 NormalX=0 NormalY=0 NormalZ=1 AngleXU=0 Radius=0.669574
    g12: Circle CenterX=-47.8702 CenterY=7.86769 CenterZ=0 NormalX=0 NormalY=0 NormalZ=1 AngleXU=0 Radius=0.669574
    g13: Circle CenterX=-44.0104 CenterY=7.86769 CenterZ=0 NormalX=0 NormalY=0 NormalZ=1 AngleXU=0 Radius=0.669574
    g14: Circle CenterX=-40.0717 CenterY=7.82831 CenterZ=0 NormalX=0 NormalY=0 NormalZ=1 AngleXU=0 Radius=0.669574
    g15: Circle CenterX=-55.5398 CenterY=-0.197736 CenterZ=0 NormalX=0 NormalY=0 NormalZ=1 AngleXU=0 Radius=0.669574
    g16: Circle CenterX=-51.6405 CenterY=-0.315897 CenterZ=0 NormalX=0 NormalY=0 NormalZ=1 AngleXU=0 Radius=0.669574
    g17: Circle CenterX=-47.7413 CenterY=-0.355283 CenterZ=0 NormalX=0 NormalY=0 NormalZ=1 AngleXU=0 Radius=0.669574
    g18: Circle CenterX=-43.8814 CenterY=-0.355283 CenterZ=0 NormalX=0 NormalY=0 NormalZ=1 AngleXU=0 Radius=0.669574
    g19: Circle CenterX=-39.9427 CenterY=-0.39467 CenterZ=0 NormalX=0 NormalY=0 NormalZ=1 AngleXU=0 Radius=0.669574
FEATURE [PartDesign::Pad] Pad010
  BaseFeature = -> Pad009
  Direction = (1,1,1)
  Length = 0.3
  Length2 = 100
  Profile = -> Sketch013
  Type = 0
FEATURE [Sketcher::SketchObject] Sketch014
  FullyConstrained = false
  MapMode = 5
  Placement = pos=(0,0,1) rot=(0,0,1;0rad)
  Support = -> [Pad010]
  sketch-geometry (8):
    g0: LineSegment StartX=-55.2207 StartY=-9.1238 StartZ=0 EndX=-51.8728 EndY=-9.1238 EndZ=0
    g1: LineSegment StartX=-51.8728 StartY=-9.1238 StartZ=0 EndX=-51.8728 EndY=-13.3775 EndZ=0
    g2: LineSegment StartX=-51.8728 StartY=-13.3775 StartZ=0 EndX=-55.2207 EndY=-13.3775 EndZ=0
    g3: LineSegment StartX=-55.2207 StartY=-13.3775 StartZ=0 EndX=-55.2207 EndY=-9.1238 EndZ=0
    g4: LineSegment StartX=-42.4595 StartY=-8.92687 StartZ=0 EndX=-39.0328 EndY=-8.92687 EndZ=0
    g5: LineSegment StartX=-39.0328 StartY=-8.92687 StartZ=0 EndX=-39.0328 EndY=-13.1018 EndZ=0
    g6: LineSegment StartX=-39.0328 StartY=-13.1018 StartZ=0 EndX=-42.4595 EndY=-13.1018 EndZ=0
    g7: LineSegment StartX=-42.4595 StartY=-13.1018 StartZ=0 EndX=-42.4595 EndY=-8.92687 EndZ=0
  constraints (16):
    c: Coincident(g0,g1)
    c: Coincident(g1,g2)
    c: Coincident(g2,g3)
    c: Coincident(g3,g0)
    c: Horizontal(g0)
    c: Horizontal(g2)
    c: Vertical(g1)
    c: Vertical(g3)
    c: Coincident(g4,g5)
    c: Coincident(g5,g6)
    c: Coincident(g6,g7)
    c: Coincident(g7,g4)
    c: Horizontal(g4)
    c: Horizontal(g6)
    c: Vertical(g5)
    c: Vertical(g7)
FEATURE [PartDesign::Pad] Pad011
  BaseFeature = -> Pad010
  Direction = (1,1,1)
  Length = 2.5
  Length2 = 100
  Profile = -> Sketch014
  Type = 0
FEATURE [Sketcher::SketchObject] Sketch015
  FullyConstrained = false
  MapMode = 5
  Placement = pos=(0,0,3.5) rot=(0,0,1;0rad)
  Support = -> [Pad011]
  sketch-geometry (8):
    g0: ArcOfCircle CenterX=-53.5765 CenterY=-10.5552 CenterZ=0 NormalX=0 NormalY=0 NormalZ=1 AngleXU=0 Radius=0.966037 StartAngle=2e-16 EndAngle=3.14159
    g1: ArcOfCircle CenterX=-53.5765 CenterY=-11.6706 CenterZ=0 NormalX=0 NormalY=0 NormalZ=1 AngleXU=0 Radius=0.966037 StartAngle=3.14159 EndAngle=6.28319
    g2: LineSegment StartX=-54.5425 StartY=-10.5552 StartZ=0 EndX=-54.5425 EndY=-11.6706 EndZ=0
    g3: LineSegment StartX=-52.6104 StartY=-10.5552 StartZ=0 EndX=-52.6104 EndY=-11.6706 EndZ=0
    g4: ArcOfCircle CenterX=-40.6287 CenterY=-10.3712 CenterZ=0 NormalX=0 NormalY=0 NormalZ=1 AngleXU=0 Radius=0.89737 StartAngle=3e-16 EndAngle=3.14159
    g5: ArcOfCircle CenterX=-40.6287 CenterY=-11.4763 CenterZ=0 NormalX=0 NormalY=0 NormalZ=1 AngleXU=0 Radius=0.89737 StartAngle=3.14159 EndAngle=6.28319
    g6: LineSegment StartX=-41.5261 StartY=-10.3712 StartZ=0 EndX=-41.5261 EndY=-11.4763 EndZ=0
    g7: LineSegment StartX=-39.7313 StartY=-10.3712 StartZ=0 EndX=-39.7313 EndY=-11.4763 EndZ=0
  constraints (12):
    c: Tangent(g0,g3) = 1.5708
    c: Tangent(g0,g2) = -1.5708
    c: Tangent(g2,g1) = -1.5708
    c: Tangent(g3,g1) = 1.5708
    c: Vertical(g2)
    c: Equal(g0,g1)
    c: Tangent(g4,g7) = 1.5708
    c: Tangent(g4,g6) = -1.5708
    c: Tangent(g6,g5) = -1.5708
    c: Tangent(g7,g5) = 1.5708
    c: Vertical(g6)
    c: Equal(g4,g5)
FEATURE [PartDesign::Pad] Pad012
  BaseFeature = -> Pad011
  Direction = (1,1,1)
  Length = 0.5
  Length2 = 100
  Profile = -> Sketch015
  Type = 0
FEATURE [Image::ImagePlane] ImagePlane004
  Placement = pos=(-41.3293,-2.22194,0) rot=(0.962455,0.27144,0;3.14159rad)
  XSize = 110.148
  YSize = 147.009
FEATURE [Sketcher::SketchObject] Sketch016
  FullyConstrained = false
  MapMode = 5
  Placement = pos=(0,0,0) rot=(1,0,0;3.14159rad)
  Support = -> [Pad012]
  sketch-geometry (10):
    g0: LineSegment StartX=-63.5655 StartY=0.677043 StartZ=0 EndX=-61.0365 EndY=0.677043 EndZ=0
    g1: LineSegment StartX=-61.0365 StartY=0.677043 StartZ=0 EndX=-61.0365 EndY=-9.32607 EndZ=0
    g2: LineSegment StartX=-61.0365 StartY=-9.32607 StartZ=0 EndX=-63.5655 EndY=-9.32607 EndZ=0
    g3: LineSegment StartX=-63.5655 StartY=-9.32607 StartZ=0 EndX=-63.5655 EndY=0.677043 EndZ=0
    g4: Circle CenterX=-62.5144 CenterY=4.39991 CenterZ=0 NormalX=0 NormalY=0 NormalZ=1 AngleXU=0 Radius=2.3619
    g5: Circle CenterX=-62.3768 CenterY=-12.9407 CenterZ=0 NormalX=0 NormalY=0 NormalZ=1 AngleXU=0 Radius=2.48274
    g6: LineSegment StartX=-17.8596 StartY=13.2006 StartZ=0 EndX=-8.16326 EndY=13.2006 EndZ=0
    g7: LineSegment StartX=-8.16326 StartY=13.2006 StartZ=0 EndX=-8.16326 EndY=4.17299 EndZ=0
    g8: LineSegment StartX=-8.16326 StartY=4.17299 StartZ=0 EndX=-17.8596 EndY=4.17299 EndZ=0
    g9: LineSegment StartX=-17.8596 StartY=4.17299 StartZ=0 EndX=-17.8596 EndY=13.2006 EndZ=0
  constraints (16):
    c: Coincident(g0,g1)
    c: Coincident(g1,g2)
    c: Coincident(g2,g3)
    c: Coincident(g3,g0)
    c: Horizontal(g0)
    c: Horizontal(g2)
    c: Vertical(g1)
    c: Vertical(g3)
    c: Coincident(g6,g7)
    c: Coincident(g7,g8)
    c: Coincident(g8,g9)
    c: Coincident(g9,g6)
    c: Horizontal(g6)
    c: Horizontal(g8)
    c: Vertical(g7)
    c: Vertical(g9)
FEATURE [PartDesign::Pad] Pad013
  BaseFeature = -> Pad012
  Direction = (1,1,1)
  Length = 1
  Length2 = 100
  Profile = -> Sketch016
  Type = 0
FEATURE [PartDesign::Pad] Pad014
  BaseFeature = -> Pad013
  Direction = (1,1,1)
  Length = 2
  Length2 = 100
  Profile = -> Pad013 [Face69]
  Type = 0
FEATURE [Sketcher::SketchObject] Sketch017
  ExternalGeometry = -> [Pad014]
  FullyConstrained = false
  MapMode = 5
  Placement = pos=(0,0,-1) rot=(1,0,0;3.14159rad)
  Support = -> [Pad014]
  sketch-geometry (2):
    g0: Circle CenterX=-62.513 CenterY=4.39693 CenterZ=0 NormalX=0 NormalY=0 NormalZ=1 AngleXU=0 Radius=1.30811
    g1: Circle CenterX=-62.3768 CenterY=-12.9407 CenterZ=0 NormalX=0 NormalY=0 NormalZ=1 AngleXU=0 Radius=1.30811
  constraints (1):
    c: Coincident(g1,g-4)
FEATURE [PartDesign::Pad] Pad015
  BaseFeature = -> Pad014
  Direction = (1,1,1)
  Length = 2
  Length2 = 100
  Profile = -> Sketch017
  Type = 0
FEATURE [Sketcher::SketchObject] Sketch018
  ExternalGeometry = -> [Pad015]
  FullyConstrained = true
  MapMode = 5
  Placement = pos=(0,0,-3) rot=(1,0,0;3.14159rad)
  Support = -> [Pad015]
  sketch-geometry (2):
    g0: Circle CenterX=-62.513 CenterY=4.39693 CenterZ=0 NormalX=0 NormalY=0 NormalZ=1 AngleXU=0 Radius=0.7
    g1: Circle CenterX=-62.3768 CenterY=-12.9407 CenterZ=0 NormalX=0 NormalY=0 NormalZ=1 AngleXU=0 Radius=0.7
  constraints (4):
    c: Coincident(g0,g-3)
    c: Radius(g0) = 0.7
    c: Equal(g0,g1) = 0.7
    c: Coincident(g1,g-4)
FEATURE [PartDesign::Pocket] Pocket002
  BaseFeature = -> Pad015
  Length = 2
  Length2 = 100
  Profile = -> Sketch018
  Type = 0
FEATURE [PartDesign::Fillet] Fillet
  Base = -> Pocket002 [Edge138,Edge144,Edge146,Edge147,Edge140]
  BaseFeature = -> Pocket002
  Radius = 0.6
  SupportTransform = false
FEATURE [PartDesign::Fillet] Fillet001
  Base = -> Fillet [Edge111,Edge117]
  BaseFeature = -> Fillet
  Radius = 1
  SupportTransform = false
FEATURE [PartDesign::Body] Body002  label="led板"
  Group = -> [Sketch011,Pad008,Sketch012,Pad009,Sketch013,Pad010,Sketch014,Pad011,Sketch015,Pad012,Sketch016,Pad013,Pad014,Sketch017,Pad015,Sketch018,Pocket002,Fillet,Fillet001]
  Origin = -> Origin002
  Placement = pos=(1,-3.3,-5.7) rot=(1,0,0;3.14159rad)
  Tip = -> Fillet001
FEATURE [Image::ImagePlane] ImagePlane005
  Placement = pos=(0,0,0) rot=(0,0,1;6.24479rad)
  XSize = 119.77
  YSize = 159.851
FEATURE [Sketcher::SketchObject] Sketch019
  FullyConstrained = false
  MapMode = 5
  Support = -> [XY_Plane003]
  sketch-geometry (14):
    g0: LineSegment StartX=-15.285 StartY=18.2701 StartZ=0 EndX=-14.9287 EndY=-5.91055 EndZ=0
    g1: LineSegment StartX=-14.9287 StartY=-5.91055 StartZ=0 EndX=-13.9702 EndY=-7.07024 EndZ=0
    g2: LineSegment StartX=-13.9702 StartY=-7.07024 StartZ=0 EndX=4.60004 EndY=-7.07024 EndZ=0
    g3: LineSegment StartX=4.60004 StartY=-7.07024 StartZ=0 EndX=9.35429 EndY=-2.48289 EndZ=0
    g4: LineSegment StartX=9.35429 StartY=-2.48289 StartZ=0 EndX=9.35429 EndY=20.9501 EndZ=0
    g5: LineSegment StartX=9.35429 StartY=20.9501 StartZ=0 EndX=8.62214 EndY=21.6249 EndZ=0
    g6: LineSegment StartX=8.62214 StartY=21.6249 StartZ=0 EndX=5.66707 EndY=21.6249 EndZ=0
    g7: LineSegment StartX=5.66707 StartY=21.6249 StartZ=0 EndX=5.66707 EndY=29.8645 EndZ=0
    g8: LineSegment StartX=5.66707 StartY=29.8645 StartZ=0 EndX=4.75407 EndY=30.9081 EndZ=0
    g9: LineSegment StartX=4.75407 StartY=30.9081 StartZ=0 EndX=-3.26279 EndY=30.9081 EndZ=0
    g10: LineSegment StartX=-3.26279 StartY=30.9081 StartZ=0 EndX=-15.285 EndY=18.2701 EndZ=0
    g11: Circle CenterX=-13.4378 CenterY=16.8704 CenterZ=0 NormalX=0 NormalY=0 NormalZ=1 AngleXU=0 Radius=1.13033
    g12: Circle CenterX=-13.0752 CenterY=-4.67578 CenterZ=0 NormalX=0 NormalY=0 NormalZ=1 AngleXU=0 Radius=1.13033
    g13: Circle CenterX=4.91384 CenterY=-2.59192 CenterZ=0 NormalX=0 NormalY=0 NormalZ=1 AngleXU=0 Radius=1.13033
  constraints (16):
    c: Coincident(g0,g1)
    c: Coincident(g1,g2)
    c: Horizontal(g2)
    c: Coincident(g2,g3)
    c: Coincident(g3,g4)
    c: Vertical(g4)
    c: Coincident(g4,g5)
    c: Coincident(g5,g6)
    c: Horizontal(g6)
    c: Coincident(g6,g7)
    c: Vertical(g7)
    c: Coincident(g7,g8)
    c: Coincident(g8,g9)
    c: Horizontal(g9)
    c: Coincident(g9,g10)
    c: Coincident(g10,g0)
FEATURE [PartDesign::Pad] Pad016
  Direction = (1,1,1)
  Length = 1
  Length2 = 100
  Profile = -> Sketch019
  Type = 0
FEATURE [Sketcher::SketchObject] Sketch020
  FullyConstrained = false
  MapMode = 5
  Placement = pos=(0,0,1) rot=(0,0,1;0rad)
  Support = -> [Pad016]
  sketch-geometry (16):
    g0: LineSegment StartX=-0.756476 StartY=29.8036 StartZ=0 EndX=5.14848 EndY=29.8036 EndZ=0
    g1: LineSegment StartX=5.14848 StartY=29.8036 StartZ=0 EndX=5.14848 EndY=22.6745 EndZ=0
    g2: LineSegment StartX=5.14848 StartY=22.6745 StartZ=0 EndX=-0.756476 EndY=22.6745 EndZ=0
    g3: LineSegment StartX=-0.756476 StartY=22.6745 StartZ=0 EndX=-0.756476 EndY=29.8036 EndZ=0
    g4: LineSegment StartX=-5.00516 StartY=20.0101 StartZ=0 EndX=9.32516 EndY=20.0101 EndZ=0
    g5: LineSegment StartX=9.32516 StartY=20.0101 StartZ=0 EndX=9.32516 EndY=10.9366 EndZ=0
    g6: LineSegment StartX=9.32516 StartY=10.9366 StartZ=0 EndX=-5.00516 EndY=10.9366 EndZ=0
    g7: LineSegment StartX=-5.00516 StartY=10.9366 StartZ=0 EndX=-5.00516 EndY=20.0101 EndZ=0
    g8: LineSegment StartX=-4.50954 StartY=8.94204 StartZ=0 EndX=8.53234 EndY=8.94204 EndZ=0
    g9: LineSegment StartX=8.53234 StartY=8.94204 StartZ=0 EndX=8.53234 EndY=1.4726 EndZ=0
    g10: LineSegment StartX=8.53234 StartY=1.4726 StartZ=0 EndX=-4.50954 EndY=1.4726 EndZ=0
    g11: LineSegment StartX=-4.50954 StartY=1.4726 StartZ=0 EndX=-4.50954 EndY=8.94204 EndZ=0
    g12: LineSegment StartX=-14.3873 StartY=6.72623 StartZ=0 EndX=-11.8456 EndY=6.72623 EndZ=0
    g13: LineSegment StartX=-11.8456 StartY=6.72623 StartZ=0 EndX=-11.8456 EndY=0.246333 EndZ=0
    g14: LineSegment StartX=-11.8456 StartY=0.246333 StartZ=0 EndX=-14.3873 EndY=0.246333 EndZ=0
    g15: LineSegment StartX=-14.3873 StartY=0.246333 StartZ=0 EndX=-14.3873 EndY=6.72623 EndZ=0
  constraints (32):
    c: Coincident(g0,g1)
    c: Coincident(g1,g2)
    c: Coincident(g2,g3)
    c: Coincident(g3,g0)
    c: Horizontal(g0)
    c: Horizontal(g2)
    c: Vertical(g1)
    c: Vertical(g3)
    c: Coincident(g4,g5)
    c: Coincident(g5,g6)
    c: Coincident(g6,g7)
    c: Coincident(g7,g4)
    c: Horizontal(g4)
    c: Horizontal(g6)
    c: Vertical(g5)
    c: Vertical(g7)
    c: Coincident(g8,g9)
    c: Coincident(g9,g10)
    c: Coincident(g10,g11)
    c: Coincident(g11,g8)
    c: Horizontal(g8)
    c: Horizontal(g10)
    c: Vertical(g9)
    c: Vertical(g11)
    c: Coincident(g12,g13)
    c: Coincident(g13,g14)
    c: Coincident(g14,g15)
    c: Coincident(g15,g12)
    c: Horizontal(g12)
    c: Horizontal(g14)
    c: Vertical(g13)
    c: Vertical(g15)
FEATURE [PartDesign::Pad] Pad017
  BaseFeature = -> Pad016
  Direction = (1,1,1)
  Length = 1
  Length2 = 100
  Profile = -> Sketch020
  Type = 0
FEATURE [PartDesign::Pad] Pad018
  BaseFeature = -> Pad017
  Direction = (1,1,1)
  Length = 6.2
  Length2 = 100
  Profile = -> Pad017 [Face36]
  Type = 0
FEATURE [PartDesign::Pad] Pad019
  BaseFeature = -> Pad018
  Direction = (1,1,1)
  Length = 10
  Length2 = 100
  Profile = -> Pad018 [Face35]
  Type = 0
FEATURE [PartDesign::Pad] Pad020
  BaseFeature = -> Pad019
  Direction = (1,1,1)
  Length = 3.5
  Length2 = 100
  Profile = -> Pad019 [Face34]
  Type = 0
FEATURE [Sketcher::SketchObject] Sketch021
  FullyConstrained = false
  MapMode = 5
  Placement = pos=(-5.00516,0,0) rot=(0.57735,-0.57735,-0.57735;2.0944rad)
  Support = -> [Pad020]
  sketch-geometry (5):
    g0: ArcOfCircle CenterX=-15.4866 CenterY=7.466 CenterZ=0 NormalX=0 NormalY=0 NormalZ=1 AngleXU=0 Radius=4.57935 StartAngle=6.25274 EndAngle=9.43406
    g1: LineSegment StartX=-20.0657 StartY=7.4235 StartZ=0 EndX=-23.0861 EndY=11.4427 EndZ=0
    g2: LineSegment StartX=-23.0861 StartY=11.4427 StartZ=0 EndX=-16.4897 EndY=15.337 EndZ=0
    g3: LineSegment StartX=-16.4897 StartY=15.337 StartZ=0 EndX=-4.99237 EndY=12.5024 EndZ=0
    g4: LineSegment StartX=-4.99237 StartY=12.5024 StartZ=0 EndX=-10.9094 EndY=7.32661 EndZ=0
  constraints (5):
    c: Coincident(g1,g2)
    c: Coincident(g2,g3)
    c: Coincident(g3,g4)
    c: Coincident(g0,g4)
    c: Coincident(g0,g1)
FEATURE [PartDesign::Pocket] Pocket003
  BaseFeature = -> Pad020
  Length = 11
  Length2 = 100
  Profile = -> Sketch021
  Type = 0
FEATURE [Sketcher::SketchObject] Sketch022
  FullyConstrained = false
  MapMode = 5
  Placement = pos=(5.14848,0,0) rot=(0.57735,0.57735,0.57735;2.0944rad)
  Support = -> [Pocket003]
  sketch-geometry (1):
    g0: Circle CenterX=26.4023 CenterY=5.29907 CenterZ=0 NormalX=0 NormalY=0 NormalZ=1 AngleXU=0 Radius=1.91
  constraints (1):
    c: Radius(g0) = 1.91
FEATURE [PartDesign::Pad] Pad021
  BaseFeature = -> Pocket003
  Direction = (1,1,1)
  Length = 3.5
  Length2 = 100
  Profile = -> Sketch022
  Type = 0
FEATURE [Sketcher::SketchObject] Sketch023
  FullyConstrained = false
  MapMode = 5
  Placement = pos=(8.53234,0,0) rot=(0.57735,0.57735,0.57735;2.0944rad)
  Support = -> [Pad021]
  sketch-geometry (2):
    g0: Circle CenterX=5.30699 CenterY=3.25014 CenterZ=0 NormalX=0 NormalY=0 NormalZ=1 AngleXU=0 Radius=2.22864
    g1: Circle CenterX=5.30699 CenterY=3.25014 CenterZ=0 NormalX=0 NormalY=0 NormalZ=1 AngleXU=0 Radius=1.76838
  constraints (1):
    c: Coincident(g1,g0)
FEATURE [PartDesign::Pad] Pad022
  BaseFeature = -> Pad021
  Direction = (1,1,1)
  Length = 2
  Length2 = 100
  Profile = -> Sketch023
  Type = 0
FEATURE [PartDesign::Body] Body003  label="电源板"
  Group = -> [Sketch019,Pad016,Sketch020,Pad017,Pad018,Pad019,Pad020,Sketch021,Pocket003,Sketch022,Pad021,Sketch023,Pad022]
  Origin = -> Origin003
  Placement = pos=(18.8,4.5,-4.4) rot=(0.707107,0.707107,0;3.14159rad)
  Tip = -> Pad022
FEATURE [Mesh::Feature] dji_fpv_system_plate_v0_1  label="dji-fpv-system_plate_v0.1"
  Placement = pos=(-8.2,-39.4,-23.1) rot=(1,0,0;4.71239rad)
FEATURE [Image::ImagePlane] ImagePlane006
  Placement = pos=(0,0,0) rot=(0,0,1;4.69668rad)
  XSize = 145.042
  YSize = 108.85
FEATURE [Sketcher::SketchObject] Sketch024
  FullyConstrained = false
  MapMode = 5
  Support = -> [XY_Plane004]
  sketch-geometry (6):
    g0: LineSegment StartX=-12.7522 StartY=28.7834 StartZ=0 EndX=11.5164 EndY=28.7834 EndZ=0
    g1: LineSegment StartX=11.5164 StartY=28.7834 StartZ=0 EndX=22.4533 EndY=17.8164 EndZ=0
    g2: LineSegment StartX=22.4533 StartY=17.8164 StartZ=0 EndX=22.4533 EndY=-27.3004 EndZ=0
    g3: LineSegment StartX=22.4533 StartY=-27.3004 StartZ=0 EndX=-24.2584 EndY=-27.3004 EndZ=0
    g4: LineSegment StartX=-24.2584 StartY=-27.3004 StartZ=0 EndX=-24.2584 EndY=18.1811 EndZ=0
    g5: LineSegment StartX=-24.2584 StartY=18.1811 StartZ=0 EndX=-12.7522 EndY=28.7834 EndZ=0
  constraints (10):
    c: Horizontal(g0)
    c: Coincident(g0,g1)
    c: Coincident(g1,g2)
    c: Vertical(g2)
    c: Coincident(g2,g3)
    c: Horizontal(g3)
    c: Coincident(g3,g4)
    c: Vertical(g4)
    c: Coincident(g4,g5)
    c: Coincident(g5,g0)
FEATURE [PartDesign::Pad] Pad023
  Direction = (1,1,1)
  Length = 2.7
  Length2 = 100
  Profile = -> Sketch024
  Type = 0
FEATURE [Sketcher::SketchObject] Sketch025
  FullyConstrained = false
  MapMode = 5
  Placement = pos=(0,0,2.7) rot=(0,0,1;0rad)
  Support = -> [Pad023]
  sketch-geometry (4):
    g0: LineSegment StartX=-23.4235 StartY=10.5781 StartZ=0 EndX=22.0587 EndY=10.5781 EndZ=0
    g1: LineSegment StartX=22.0587 StartY=10.5781 StartZ=0 EndX=22.0587 EndY=-14.8928 EndZ=0
    g2: LineSegment StartX=22.0587 StartY=-14.8928 StartZ=0 EndX=-23.4235 EndY=-14.8928 EndZ=0
    g3: LineSegment StartX=-23.4235 StartY=-14.8928 StartZ=0 EndX=-23.4235 EndY=10.5781 EndZ=0
  constraints (8):
    c: Coincident(g0,g1)
    c: Coincident(g1,g2)
    c: Coincident(g2,g3)
    c: Coincident(g3,g0)
    c: Horizontal(g0)
    c: Horizontal(g2)
    c: Vertical(g1)
    c: Vertical(g3)
FEATURE [PartDesign::Pocket] Pocket004
  BaseFeature = -> Pad023
  Length = 0.1
  Length2 = 100
  Profile = -> Sketch025
  Type = 0
FEATURE [Image::ImagePlane] ImagePlane007
  Placement = pos=(-2.01044,-1.9895,0) rot=(-0.705253,0.708956,0;3.14159rad)
  XSize = 152.472
  YSize = 114.426
FEATURE [Sketcher::SketchObject] Sketch026
  FullyConstrained = false
  MapMode = 5
  Placement = pos=(0,0,0) rot=(1,0,0;3.14159rad)
  Support = -> [Pocket004]
  sketch-geometry (4):
    g0: LineSegment StartX=-6.36871 StartY=19.9158 StartZ=0 EndX=5.15631 EndY=19.9158 EndZ=0
    g1: LineSegment StartX=5.15631 StartY=19.9158 StartZ=0 EndX=5.15631 EndY=17.2241 EndZ=0
    g2: LineSegment StartX=5.15631 StartY=17.2241 StartZ=0 EndX=-6.36871 EndY=17.2241 EndZ=0
    g3: LineSegment StartX=-6.36871 StartY=17.2241 StartZ=0 EndX=-6.36871 EndY=19.9158 EndZ=0
  constraints (8):
    c: Coincident(g0,g1)
    c: Coincident(g1,g2)
    c: Coincident(g2,g3)
    c: Coincident(g3,g0)
    c: Horizontal(g0)
    c: Horizontal(g2)
    c: Vertical(g1)
    c: Vertical(g3)
FEATURE [PartDesign::Pad] Pad024
  BaseFeature = -> Pocket004
  Direction = (1,1,1)
  Length = 1
  Length2 = 100
  Profile = -> Sketch026
  Type = 0
FEATURE [Sketcher::SketchObject] Sketch027
  FullyConstrained = false
  MapMode = 5
  Placement = pos=(0,0,0) rot=(1,0,0;3.14159rad)
  Support = -> [Pad024]
  sketch-geometry (4):
    g0: LineSegment StartX=-24.0712 StartY=26.2813 StartZ=0 EndX=21.9965 EndY=26.2813 EndZ=0
    g1: LineSegment StartX=21.9965 StartY=26.2813 StartZ=0 EndX=21.9965 EndY=11.6004 EndZ=0
    g2: LineSegment StartX=21.9965 StartY=11.6004 StartZ=0 EndX=-24.0712 EndY=11.6004 EndZ=0
    g3: LineSegment StartX=-24.0712 StartY=11.6004 StartZ=0 EndX=-24.0712 EndY=26.2813 EndZ=0
  constraints (8):
    c: Coincident(g0,g1)
    c: Coincident(g1,g2)
    c: Coincident(g2,g3)
    c: Coincident(g3,g0)
    c: Horizontal(g0)
    c: Horizontal(g2)
    c: Vertical(g1)
    c: Vertical(g3)
FEATURE [PartDesign::Pad] Pad025
  BaseFeature = -> Pad024
  Direction = (1,1,1)
  Length = 0.2
  Length2 = 100
  Profile = -> Sketch027
  Type = 0
FEATURE [PartDesign::Body] Body004  label="屏幕"
  Group = -> [Sketch024,Pad023,Sketch025,Pocket004,Sketch026,Pad024,Sketch027,Pad025]
  Origin = -> Origin004
  Tip = -> Pad025
FEATURE [Sketcher::SketchObject] Sketch028
  FullyConstrained = false
  MapMode = 5
  Support = -> [XY_Plane005]
  sketch-geometry (6):
    g0: LineSegment StartX=-13.0741 StartY=32.5167 StartZ=0 EndX=-26.6389 EndY=19.1061 EndZ=0
    g1: LineSegment StartX=-26.6389 StartY=19.1061 StartZ=0 EndX=-26.6389 EndY=-29.4495 EndZ=0
    g2: LineSegment StartX=-26.6389 StartY=-29.4495 StartZ=0 EndX=24.8455 EndY=-29.4495 EndZ=0
    g3: LineSegment StartX=24.8455 StartY=-29.4495 StartZ=0 EndX=24.8455 EndY=19.5685 EndZ=0
    g4: LineSegment StartX=24.8455 StartY=19.5685 StartZ=0 EndX=11.3136 EndY=32.5167 EndZ=0
    g5: LineSegment StartX=11.3136 StartY=32.5167 StartZ=0 EndX=-13.0741 EndY=32.5167 EndZ=0
  constraints (10):
    c: Coincident(g0,g1)
    c: Vertical(g1)
    c: Coincident(g1,g2)
    c: Horizontal(g2)
    c: Coincident(g2,g3)
    c: Vertical(g3)
    c: Coincident(g3,g4)
    c: Coincident(g4,g5)
    c: Coincident(g5,g0)
    c: Horizontal(g5)
FEATURE [PartDesign::Pad] Pad026
  Direction = (1,1,1)
  Length = 5
  Length2 = 100
  Profile = -> Sketch028
  Type = 0
FEATURE [Sketcher::SketchObject] Sketch029
  FullyConstrained = false
  MapMode = 5
  Placement = pos=(0,0,5) rot=(0,0,1;0rad)
  Support = -> [Pad026]
  sketch-geometry (6):
    g0: LineSegment StartX=-25.0333 StartY=18.4644 StartZ=0 EndX=-13.0812 EndY=29.4209 EndZ=0
    g1: LineSegment StartX=-13.0812 StartY=29.4209 StartZ=0 EndX=11.7837 EndY=29.4209 EndZ=0
    g2: LineSegment StartX=11.7837 StartY=29.4209 StartZ=0 EndX=23.0041 EndY=17.8542 EndZ=0
    g3: LineSegment StartX=23.0041 StartY=17.8542 StartZ=0 EndX=23.0041 EndY=-28.0221 EndZ=0
    g4: LineSegment StartX=23.0041 StartY=-28.0221 StartZ=0 EndX=-25.0333 EndY=-28.0221 EndZ=0
    g5: LineSegment StartX=-25.0333 StartY=-28.0221 StartZ=0 EndX=-25.0333 EndY=18.4644 EndZ=0
  constraints (10):
    c: Coincident(g0,g1)
    c: Horizontal(g1)
    c: Coincident(g1,g2)
    c: Coincident(g2,g3)
    c: Vertical(g3)
    c: Coincident(g3,g4)
    c: Horizontal(g4)
    c: Coincident(g4,g5)
    c: Coincident(g5,g0)
    c: Vertical(g5)
FEATURE [PartDesign::Pocket] Pocket005
  BaseFeature = -> Pad026
  Length = 4
  Length2 = 100
  Profile = -> Sketch029
  Type = 0
FEATURE [Sketcher::SketchObject] Sketch030
  FullyConstrained = false
  MapMode = 5
  Placement = pos=(0,0,0) rot=(1,0,0;3.14159rad)
  Support = -> [Pocket005]
  sketch-geometry (4):
    g0: LineSegment StartX=-9.87384 StartY=22.6 StartZ=0 EndX=9.44818 EndY=22.6 EndZ=0
    g1: LineSegment StartX=9.44818 StartY=22.6 StartZ=0 EndX=9.44818 EndY=14.3339 EndZ=0
    g2: LineSegment StartX=9.44818 StartY=14.3339 StartZ=0 EndX=-9.87384 EndY=14.3339 EndZ=0
    g3: LineSegment StartX=-9.87384 StartY=14.3339 StartZ=0 EndX=-9.87384 EndY=22.6 EndZ=0
  constraints (8):
    c: Coincident(g0,g1)
    c: Coincident(g1,g2)
    c: Coincident(g2,g3)
    c: Coincident(g3,g0)
    c: Horizontal(g0)
    c: Horizontal(g2)
    c: Vertical(g1)
    c: Vertical(g3)
FEATURE [PartDesign::Pocket] Pocket006
  BaseFeature = -> Pocket005
  Length = 5
  Length2 = 100
  Profile = -> Sketch030
  Type = 0
FEATURE [PartDesign::Body] Body005  label="屏幕壳"
  Group = -> [Sketch028,Pad026,Sketch029,Pocket005,Sketch030,Pocket006]
  Origin = -> Origin005
  Tip = -> Pocket006
FEATURE [Image::ImagePlane] ImagePlane008
  Placement = pos=(0,0,0) rot=(0,0,1;1.93731rad)
  XSize = 28.7733
  YSize = 62.2752
FEATURE [Sketcher::SketchObject] Sketch031
  FullyConstrained = false
  MapMode = 5
  Support = -> [XY_Plane006]
  sketch-geometry (18):
    g0: LineSegment StartX=-15.8241 StartY=0.702012 StartZ=0 EndX=-16.1041 EndY=-0.397312 EndZ=0
    g1: LineSegment StartX=-16.1041 StartY=-0.397312 StartZ=0 EndX=-16.1041 EndY=-9.62247 EndZ=0
    g2: LineSegment StartX=-16.1041 StartY=-9.62247 StartZ=0 EndX=-14.9173 EndY=-10.3717 EndZ=0
    g3: LineSegment StartX=-14.9173 StartY=-10.3717 StartZ=0 EndX=-14.1884 EndY=-10.6957 EndZ=0
    g4: LineSegment StartX=-14.1884 StartY=-10.6957 StartZ=0 EndX=1.80216 EndY=-10.6957 EndZ=0
    g5: LineSegment StartX=1.80216 StartY=-10.6957 StartZ=0 EndX=2.42988 EndY=-10.0996 EndZ=0
    g6: LineSegment StartX=2.42988 StartY=-10.0996 StartZ=0 EndX=6.25457 EndY=0.878554 EndZ=0
    g7: LineSegment StartX=6.25457 StartY=0.878554 StartZ=0 EndX=6.65956 EndY=1.34428 EndZ=0
    g8: LineSegment StartX=6.65956 StartY=1.34428 StartZ=0 EndX=15.2249 EndY=1.34428 EndZ=0
    g9: LineSegment StartX=15.2249 StartY=1.34428 StartZ=0 EndX=17.8206 EndY=3.64802 EndZ=0
    g10: LineSegment StartX=17.8206 StartY=3.64802 StartZ=0 EndX=17.8206 EndY=9.16611 EndZ=0
    g11: LineSegment StartX=17.8206 StartY=9.16611 StartZ=0 EndX=17.3475 EndY=10.1178 EndZ=0
    g12: LineSegment StartX=17.3475 StartY=10.1178 StartZ=0 EndX=16.497 EndY=10.7253 EndZ=0
    g13: LineSegment StartX=16.497 StartY=10.7253 StartZ=0 EndX=6.89898 EndY=10.7253 EndZ=0
    g14: LineSegment StartX=6.89898 StartY=10.7253 StartZ=0 EndX=-15.4012 EndY=1.91033 EndZ=0
    g15: LineSegment StartX=-15.4012 StartY=1.91033 StartZ=0 EndX=-15.8241 EndY=0.702012 EndZ=0
    g16: Circle CenterX=-13.7541 CenterY=-8.51295 CenterZ=0 NormalX=0 NormalY=0 NormalZ=1 AngleXU=0 Radius=1.01183
    g17: Circle CenterX=6.16374 CenterY=6.54824 CenterZ=0 NormalX=0 NormalY=0 NormalZ=1 AngleXU=0 Radius=1.01183
  constraints (21):
    c: Coincident(g0,g1)
    c: Vertical(g1)
    c: Coincident(g1,g2)
    c: Coincident(g2,g3)
    c: Coincident(g3,g4)
    c: Horizontal(g4)
    c: Coincident(g4,g5)
    c: Coincident(g5,g6)
    c: Coincident(g6,g7)
    c: Coincident(g7,g8)
    c: Horizontal(g8)
    c: Coincident(g8,g9)
    c: Coincident(g9,g10)
    c: Vertical(g10)
    c: Coincident(g10,g11)
    c: Coincident(g11,g12)
    c: Coincident(g12,g13)
    c: Horizontal(g13)
    c: Coincident(g13,g14)
    c: Coincident(g14,g15)
    c: Coincident(g15,g0)
FEATURE [PartDesign::Pad] Pad027
  Direction = (1,1,1)
  Length = 1
  Length2 = 100
  Profile = -> Sketch031
  Type = 0
FEATURE [Sketcher::SketchObject] Sketch032
  FullyConstrained = false
  MapMode = 5
  Placement = pos=(0,0,1) rot=(0,0,1;0rad)
  Support = -> [Pad027]
  sketch-geometry (16):
    g0: LineSegment StartX=-10.5977 StartY=-2.32632 StartZ=0 EndX=-6.18128 EndY=-2.32632 EndZ=0
    g1: LineSegment StartX=-6.18128 StartY=-2.32632 StartZ=0 EndX=-6.18128 EndY=-5.7062 EndZ=0
    g2: LineSegment StartX=-6.18128 StartY=-5.7062 StartZ=0 EndX=-10.5977 EndY=-5.7062 EndZ=0
    g3: LineSegment StartX=-10.5977 StartY=-5.7062 StartZ=0 EndX=-10.5977 EndY=-2.32632 EndZ=0
    g4: LineSegment StartX=-0.548157 StartY=2.13538 StartZ=0 EndX=3.82325 EndY=2.13538 EndZ=0
    g5: LineSegment StartX=3.82325 StartY=2.13538 StartZ=0 EndX=3.82325 EndY=-1.33489 EndZ=0
    g6: LineSegment StartX=3.82325 StartY=-1.33489 StartZ=0 EndX=-0.548157 EndY=-1.33489 EndZ=0
    g7: LineSegment StartX=-0.548157 StartY=-1.33489 StartZ=0 EndX=-0.548157 EndY=2.13538 EndZ=0
    g8: LineSegment StartX=9.09025 StartY=7.23703 StartZ=0 EndX=12.2896 EndY=10.4769 EndZ=0
    g9: LineSegment StartX=12.2896 StartY=10.4769 StartZ=0 EndX=14.4967 EndY=10.5579 EndZ=0
    g10: LineSegment StartX=14.4967 StartY=10.5579 StartZ=0 EndX=17.6961 EndY=7.33827 EndZ=0
    g11: LineSegment StartX=17.6961 StartY=7.33827 StartZ=0 EndX=17.6961 EndY=5.33362 EndZ=0
    g12: LineSegment StartX=17.6961 StartY=5.33362 StartZ=0 EndX=14.5777 EndY=2.07353 EndZ=0
    g13: LineSegment StartX=14.5777 StartY=2.07353 StartZ=0 EndX=12.7351 EndY=2.07353 EndZ=0
    g14: LineSegment StartX=12.7351 StartY=2.07353 StartZ=0 EndX=9.09025 EndY=5.35387 EndZ=0
    g15: LineSegment StartX=9.09025 StartY=5.35387 StartZ=0 EndX=9.09025 EndY=7.23703 EndZ=0
  constraints (27):
    c: Coincident(g0,g1)
    c: Coincident(g1,g2)
    c: Coincident(g2,g3)
    c: Coincident(g3,g0)
    c: Horizontal(g0)
    c: Horizontal(g2)
    c: Vertical(g1)
    c: Vertical(g3)
    c: Coincident(g4,g5)
    c: Coincident(g5,g6)
    c: Coincident(g6,g7)
    c: Coincident(g7,g4)
    c: Horizontal(g4)
    c: Horizontal(g6)
    c: Vertical(g5)
    c: Vertical(g7)
    c: Coincident(g8,g9)
    c: Coincident(g9,g10)
    c: Coincident(g10,g11)
    c: Vertical(g11)
    c: Coincident(g11,g12)
    c: Coincident(g12,g13)
    c: Horizontal(g13)
    c: Coincident(g13,g14)
    c: Coincident(g14,g15)
    c: Coincident(g15,g8)
    c: Vertical(g15)
FEATURE [PartDesign::Pad] Pad028
  BaseFeature = -> Pad027
  Direction = (1,1,1)
  Length = 3
  Length2 = 100
  Profile = -> Sketch032
  Type = 0
FEATURE [Sketcher::SketchObject] Sketch033
  FullyConstrained = true
  MapMode = 5
  Placement = pos=(0,0,4) rot=(0,0,1;0rad)
  Support = -> [Pad028]
FEATURE [PartDesign::Pad] Pad029
  BaseFeature = -> Pad028
  Direction = (1,1,1)
  Length = 2.3
  Length2 = 100
  Profile = -> Pad028 [Face39]
  Type = 0
FEATURE [Sketcher::SketchObject] Sketch034
  FullyConstrained = false
  MapMode = 5
  Placement = pos=(0,0,6.3) rot=(0,0,1;0rad)
  Support = -> [Pad029]
  sketch-geometry (1):
    g0: Circle CenterX=13.3674 CenterY=6.58018 CenterZ=0 NormalX=0 NormalY=0 NormalZ=1 AngleXU=0 Radius=2.2045
FEATURE [PartDesign::Pad] Pad030
  BaseFeature = -> Pad029
  Direction = (1,1,1)
  Length = 4
  Length2 = 100
  Profile = -> Sketch034
  Type = 0
FEATURE [Sketcher::SketchObject] Sketch035
  FullyConstrained = false
  MapMode = 5
  Placement = pos=(0,0,10.3) rot=(0,0,1;0rad)
  Support = -> [Pad030]
  sketch-geometry (1):
    g0: Circle CenterX=13.4372 CenterY=6.53388 CenterZ=0 NormalX=0 NormalY=0 NormalZ=1 AngleXU=0 Radius=3.42431
FEATURE [PartDesign::Pad] Pad031
  BaseFeature = -> Pad030
  Direction = (1,1,1)
  Length = 2
  Length2 = 100
  Profile = -> Sketch035
  Reversed = true
  Type = 0
FEATURE [Sketcher::SketchObject] Sketch036
  FullyConstrained = false
  MapMode = 5
  Placement = pos=(0,0,4) rot=(0,0,1;0rad)
  Support = -> [Pad031]
  sketch-geometry (6):
    g0: Circle CenterX=1.72428 CenterY=0.373466 CenterZ=0 NormalX=0 NormalY=0 NormalZ=1 AngleXU=0 Radius=1.26809
    g1: Circle CenterX=-8.45018 CenterY=-4.09433 CenterZ=0 NormalX=0 NormalY=0 NormalZ=1 AngleXU=0 Radius=1.26809
    g2: LineSegment StartX=-13.3419 StartY=4.50003 StartZ=0 EndX=5.17994 EndY=4.50003 EndZ=0
    g3: LineSegment StartX=5.17994 StartY=4.50003 StartZ=0 EndX=5.17994 EndY=-8.4874 EndZ=0
    g4: LineSegment StartX=5.17994 StartY=-8.4874 StartZ=0 EndX=-13.3419 EndY=-8.4874 EndZ=0
    g5: LineSegment StartX=-13.3419 StartY=-8.4874 StartZ=0 EndX=-13.3419 EndY=4.50003 EndZ=0
  constraints (8):
    c: Coincident(g2,g3)
    c: Coincident(g3,g4)
    c: Coincident(g4,g5)
    c: Coincident(g5,g2)
    c: Horizontal(g2)
    c: Horizontal(g4)
    c: Vertical(g3)
    c: Vertical(g5)
FEATURE [PartDesign::Pocket] Pocket007
  BaseFeature = -> Pad031
  Length = 1
  Length2 = 100
  Profile = -> Sketch036
  Type = 0
FEATURE [PartDesign::Body] Body006  label="按键板"
  Group = -> [Sketch031,Pad027,Sketch032,Pad028,Sketch033,Pad029,Sketch034,Pad030,Sketch035,Pad031,Sketch036,Pocket007]
  Origin = -> Origin006
  Tip = -> Pocket007
FEATURE [Sketcher::SketchObject] Sketch037
  FullyConstrained = true
  MapMode = 5
  Support = -> [XY_Plane007]
  sketch-geometry (1):
    g0: Circle CenterX=0 CenterY=0 CenterZ=0 NormalX=0 NormalY=0 NormalZ=1 AngleXU=0 Radius=4.9
  constraints (2):
    c: Coincident(g0,g-1)
    c: Diameter(g0) = 9.8
FEATURE [PartDesign::Pad] Pad032
  Direction = (1,1,1)
  Length = 5
  Length2 = 100
  Profile = -> Sketch037
  Type = 0
FEATURE [Sketcher::SketchObject] Sketch038
  FullyConstrained = true
  MapMode = 5
  Placement = pos=(0,0,5) rot=(0,0,1;0rad)
  Support = -> [Pad032]
  sketch-geometry (1):
    g0: Circle CenterX=0 CenterY=0 CenterZ=0 NormalX=0 NormalY=0 NormalZ=1 AngleXU=0 Radius=6.1
  constraints (2):
    c: Coincident(g0,g-1)
    c: Diameter(g0) = 12.2
FEATURE [PartDesign::Pad] Pad033
  BaseFeature = -> Pad032
  Direction = (1,1,1)
  Length = 2.4
  Length2 = 100
  Profile = -> Sketch038
  Type = 0
FEATURE [PartDesign::Fillet] Fillet002
  Base = -> Pad033 [Edge3,Edge2]
  BaseFeature = -> Pad033
  Radius = 1
  SupportTransform = false
FEATURE [PartDesign::Fillet] Fillet003
  Base = -> Fillet002 [Edge10]
  BaseFeature = -> Fillet002
  Radius = 0.5
  SupportTransform = false
FEATURE [Sketcher::SketchObject] Sketch039
  FullyConstrained = true
  MapMode = 5
  Placement = pos=(0,0,7.4) rot=(0,0,1;0rad)
  Support = -> [Fillet003]
  sketch-geometry (1):
    g0: Circle CenterX=0 CenterY=0 CenterZ=0 NormalX=0 NormalY=0 NormalZ=1 AngleXU=0 Radius=6.75
  constraints (2):
    c: Coincident(g0,g-1)
    c: Diameter(g0) = 13.5
FEATURE [PartDesign::Pad] Pad034
  BaseFeature = -> Fillet003
  Direction = (1,1,1)
  Length = 37.5
  Length2 = 100
  Profile = -> Sketch039
  Type = 0
FEATURE [PartDesign::Fillet] Fillet004
  Base = -> Pad034 [Edge3]
  BaseFeature = -> Pad034
  Radius = 4
  SupportTransform = false
FEATURE [PartDesign::Chamfer] Chamfer
  Angle = 45
  Base = -> Fillet004 [Edge3]
  BaseFeature = -> Fillet004
  ChamferType = 0
  FlipDirection = false
  Size = 1
  Size2 = 1
  SupportTransform = false
FEATURE [PartDesign::Chamfer] Chamfer001
  Angle = 45
  Base = -> Chamfer [Edge2]
  BaseFeature = -> Chamfer
  ChamferType = 0
  FlipDirection = false
  Size = 1
  Size2 = 1
  SupportTransform = false
FEATURE [PartDesign::Chamfer] Chamfer002
  Angle = 45
  Base = -> Chamfer001 [Edge2]
  BaseFeature = -> Chamfer001
  ChamferType = 0
  FlipDirection = false
  Size = 1
  Size2 = 1
  SupportTransform = false
FEATURE [Sketcher::SketchObject] Sketch040
  FullyConstrained = true
  MapMode = 5
  Placement = pos=(0,0,0) rot=(1,0,0;3.14159rad)
  Support = -> [Chamfer002]
  sketch-geometry (1):
    g0: Circle CenterX=0 CenterY=0 CenterZ=0 NormalX=0 NormalY=0 NormalZ=1 AngleXU=0 Radius=3.05
  constraints (2):
    c: Coincident(g0,g-1)
    c: Diameter(g0) = 6.1
FEATURE [PartDesign::Pocket] Pocket008
  BaseFeature = -> Chamfer002
  Length = 6
  Length2 = 100
  Profile = -> Sketch040
  Type = 0
FEATURE [PartDesign::Fillet] Fillet005
  Base = -> Pocket008 [Edge24]
  BaseFeature = -> Pocket008
  Radius = 0.3
  SupportTransform = false
FEATURE [PartDesign::Body] Body007  label="天线"
  Group = -> [Sketch037,Pad032,Sketch038,Pad033,Fillet002,Fillet003,Sketch039,Pad034,Fillet004,Chamfer,Chamfer001,Chamfer002,Sketch040,Pocket008,Fillet005]
  Origin = -> Origin007
  Tip = -> Fillet005
